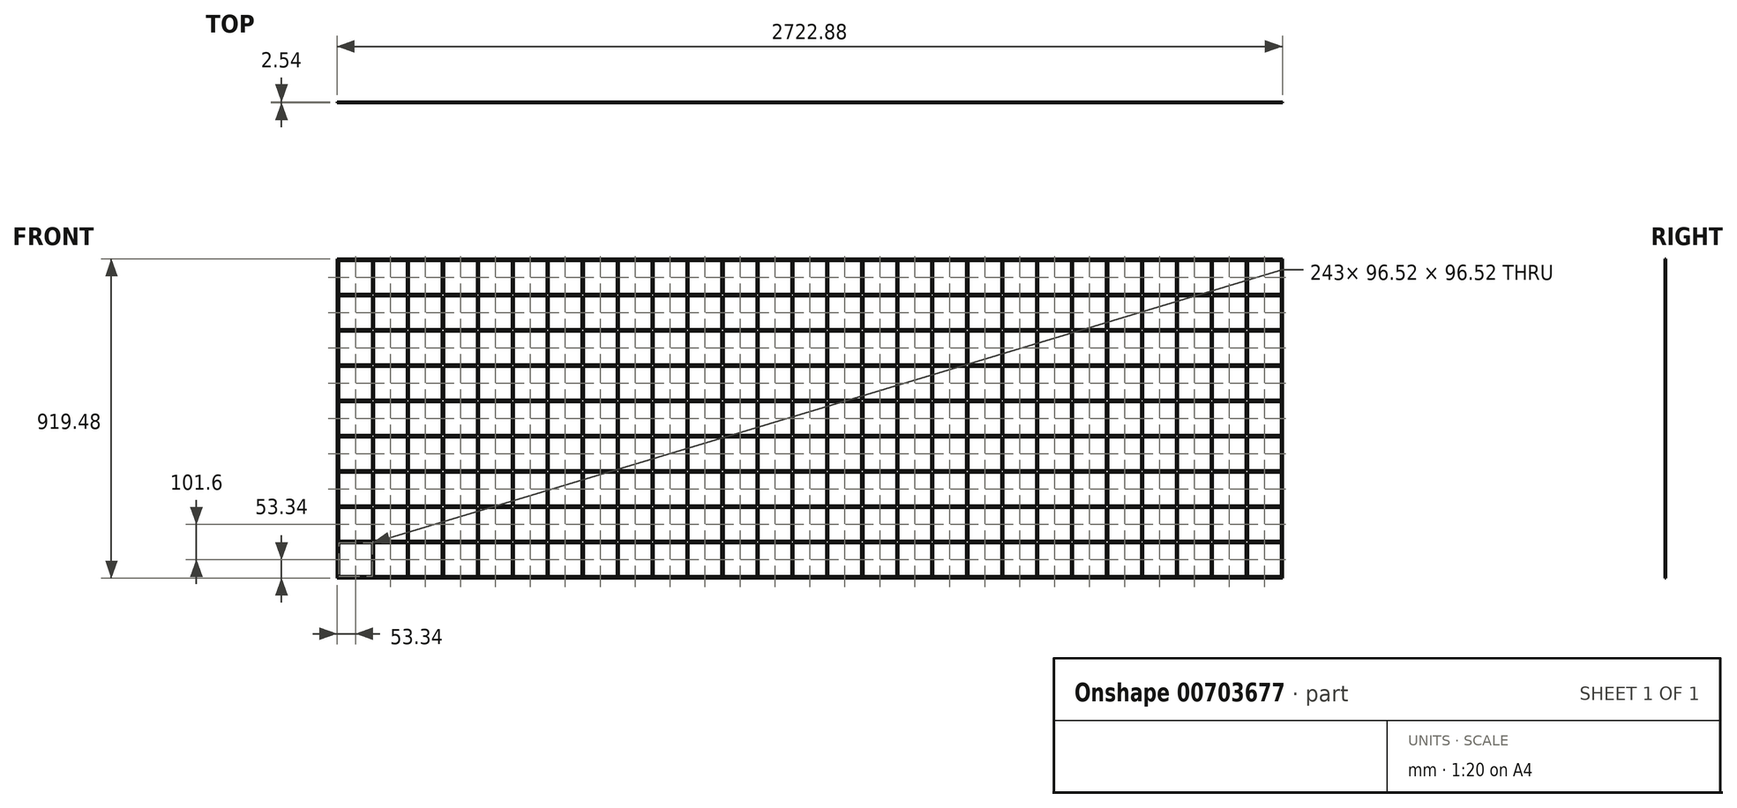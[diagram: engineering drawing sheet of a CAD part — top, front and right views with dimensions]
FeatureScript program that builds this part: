
annotation { "Feature Type Name" : "Feature", "Feature Type Description" : "" }
export const myFeature = defineFeature(function(context is Context, id is Id, definition is map)
    precondition{}
    {
        {
            var Q0;
            Q0=qCreatedBy(makeId("Front.planeOp"),FACE);
            var sketch = newSketch(context, id + "F0", { "sketchPlane" : qUnion([Q0])});
            skLineSegment(sketch, "E0.bottom", {"start": v(0, 0) * mm, "end": v(2722.88, 0) * mm});
            skLineSegment(sketch, "E0.top", {"start": v(0, 919.48) * mm, "end": v(2722.88, 919.48) * mm});
            skLineSegment(sketch, "E0.left", {"start": v(0, 0) * mm, "end": v(0, 919.48) * mm});
            skLineSegment(sketch, "E0.right", {"start": v(2722.88, 0) * mm, "end": v(2722.88, 919.48) * mm});
            skSolve(sketch);
        }
        {
            var Q0;
            Q0=qSketchRegion(id+"F0",true);
            extrude(context, id + "F1", {"entities" : qUnion([Q0]), "depth" : 2.54 * mm, "offsetDistance" : 25.4 * mm});
        }
        {
            var Q0;
            Q0=makeQuery(id+"F0.imprint","IMPRINT",FACE,{"disambiguationData":[TD([[makeQuery(id+"F0.imprint","IMPRINT",EDGE,{"derivedFrom":sQuery(id+"F0.wireOp",EDGE,"E0.bottom")}),1.0]])]});
            var sketch = newSketch(context, id + "F2", { "sketchPlane" : qUnion([Q0])});
            skLineSegment(sketch, "E1.bottom", {"start": v(5.08, 914.4) * mm, "end": v(101.6, 914.4) * mm});
            skLineSegment(sketch, "E1.top", {"start": v(5.08, 817.88) * mm, "end": v(101.6, 817.88) * mm});
            skLineSegment(sketch, "E1.left", {"start": v(5.08, 914.4) * mm, "end": v(5.08, 817.88) * mm});
            skLineSegment(sketch, "E1.right", {"start": v(101.6, 914.4) * mm, "end": v(101.6, 817.88) * mm});
            skLineSegment(sketch, "E2.0.1.0", {"start": v(101.6, 812.8) * mm, "end": v(101.6, 716.28) * mm});
            skLineSegment(sketch, "E2.0.1.1", {"start": v(5.08, 812.8) * mm, "end": v(101.6, 812.8) * mm});
            skLineSegment(sketch, "E2.0.1.2", {"start": v(5.08, 812.8) * mm, "end": v(5.08, 716.28) * mm});
            skLineSegment(sketch, "E2.0.1.3", {"start": v(5.08, 716.28) * mm, "end": v(101.6, 716.28) * mm});
            skLineSegment(sketch, "E2.0.2.0", {"start": v(101.6, 711.2) * mm, "end": v(101.6, 614.68) * mm});
            skLineSegment(sketch, "E2.0.2.1", {"start": v(5.08, 711.2) * mm, "end": v(101.6, 711.2) * mm});
            skLineSegment(sketch, "E2.0.2.2", {"start": v(5.08, 711.2) * mm, "end": v(5.08, 614.68) * mm});
            skLineSegment(sketch, "E2.0.2.3", {"start": v(5.08, 614.68) * mm, "end": v(101.6, 614.68) * mm});
            skLineSegment(sketch, "E2.0.3.0", {"start": v(101.6, 609.6) * mm, "end": v(101.6, 513.08) * mm});
            skLineSegment(sketch, "E2.0.3.1", {"start": v(5.08, 609.6) * mm, "end": v(101.6, 609.6) * mm});
            skLineSegment(sketch, "E2.0.3.2", {"start": v(5.08, 609.6) * mm, "end": v(5.08, 513.08) * mm});
            skLineSegment(sketch, "E2.0.3.3", {"start": v(5.08, 513.08) * mm, "end": v(101.6, 513.08) * mm});
            skLineSegment(sketch, "E2.0.4.0", {"start": v(101.6, 508) * mm, "end": v(101.6, 411.48) * mm});
            skLineSegment(sketch, "E2.0.4.1", {"start": v(5.08, 508) * mm, "end": v(101.6, 508) * mm});
            skLineSegment(sketch, "E2.0.4.2", {"start": v(5.08, 508) * mm, "end": v(5.08, 411.48) * mm});
            skLineSegment(sketch, "E2.0.4.3", {"start": v(5.08, 411.48) * mm, "end": v(101.6, 411.48) * mm});
            skLineSegment(sketch, "E2.0.5.0", {"start": v(101.6, 406.4) * mm, "end": v(101.6, 309.88) * mm});
            skLineSegment(sketch, "E2.0.5.1", {"start": v(5.08, 406.4) * mm, "end": v(101.6, 406.4) * mm});
            skLineSegment(sketch, "E2.0.5.2", {"start": v(5.08, 406.4) * mm, "end": v(5.08, 309.88) * mm});
            skLineSegment(sketch, "E2.0.5.3", {"start": v(5.08, 309.88) * mm, "end": v(101.6, 309.88) * mm});
            skLineSegment(sketch, "E2.0.6.0", {"start": v(101.6, 304.8) * mm, "end": v(101.6, 208.28) * mm});
            skLineSegment(sketch, "E2.0.6.1", {"start": v(5.08, 304.8) * mm, "end": v(101.6, 304.8) * mm});
            skLineSegment(sketch, "E2.0.6.2", {"start": v(5.08, 304.8) * mm, "end": v(5.08, 208.28) * mm});
            skLineSegment(sketch, "E2.0.6.3", {"start": v(5.08, 208.28) * mm, "end": v(101.6, 208.28) * mm});
            skLineSegment(sketch, "E2.0.7.0", {"start": v(101.6, 203.2) * mm, "end": v(101.6, 106.68) * mm});
            skLineSegment(sketch, "E2.0.7.1", {"start": v(5.08, 203.2) * mm, "end": v(101.6, 203.2) * mm});
            skLineSegment(sketch, "E2.0.7.2", {"start": v(5.08, 203.2) * mm, "end": v(5.08, 106.68) * mm});
            skLineSegment(sketch, "E2.0.7.3", {"start": v(5.08, 106.68) * mm, "end": v(101.6, 106.68) * mm});
            skLineSegment(sketch, "E2.0.8.0", {"start": v(101.6, 101.6) * mm, "end": v(101.6, 5.08) * mm});
            skLineSegment(sketch, "E2.0.8.1", {"start": v(5.08, 101.6) * mm, "end": v(101.6, 101.6) * mm});
            skLineSegment(sketch, "E2.0.8.2", {"start": v(5.08, 101.6) * mm, "end": v(5.08, 5.08) * mm});
            skLineSegment(sketch, "E2.0.8.3", {"start": v(5.08, 5.08) * mm, "end": v(101.6, 5.08) * mm});
            skLineSegment(sketch, "E2.1.0.0", {"start": v(202.26, 914.4) * mm, "end": v(202.26, 817.88) * mm});
            skLineSegment(sketch, "E2.1.0.1", {"start": v(105.74, 914.4) * mm, "end": v(202.26, 914.4) * mm});
            skLineSegment(sketch, "E2.1.0.2", {"start": v(105.74, 914.4) * mm, "end": v(105.74, 817.88) * mm});
            skLineSegment(sketch, "E2.1.0.3", {"start": v(105.74, 817.88) * mm, "end": v(202.26, 817.88) * mm});
            skLineSegment(sketch, "E2.1.1.0", {"start": v(202.26, 812.8) * mm, "end": v(202.26, 716.28) * mm});
            skLineSegment(sketch, "E2.1.1.1", {"start": v(105.74, 812.8) * mm, "end": v(202.26, 812.8) * mm});
            skLineSegment(sketch, "E2.1.1.2", {"start": v(105.74, 812.8) * mm, "end": v(105.74, 716.28) * mm});
            skLineSegment(sketch, "E2.1.1.3", {"start": v(105.74, 716.28) * mm, "end": v(202.26, 716.28) * mm});
            skLineSegment(sketch, "E2.1.2.0", {"start": v(202.26, 711.2) * mm, "end": v(202.26, 614.68) * mm});
            skLineSegment(sketch, "E2.1.2.1", {"start": v(105.74, 711.2) * mm, "end": v(202.26, 711.2) * mm});
            skLineSegment(sketch, "E2.1.2.2", {"start": v(105.74, 711.2) * mm, "end": v(105.74, 614.68) * mm});
            skLineSegment(sketch, "E2.1.2.3", {"start": v(105.74, 614.68) * mm, "end": v(202.26, 614.68) * mm});
            skLineSegment(sketch, "E2.1.3.0", {"start": v(202.26, 609.6) * mm, "end": v(202.26, 513.08) * mm});
            skLineSegment(sketch, "E2.1.3.1", {"start": v(105.74, 609.6) * mm, "end": v(202.26, 609.6) * mm});
            skLineSegment(sketch, "E2.1.3.2", {"start": v(105.74, 609.6) * mm, "end": v(105.74, 513.08) * mm});
            skLineSegment(sketch, "E2.1.3.3", {"start": v(105.74, 513.08) * mm, "end": v(202.26, 513.08) * mm});
            skLineSegment(sketch, "E2.1.4.0", {"start": v(202.26, 508) * mm, "end": v(202.26, 411.48) * mm});
            skLineSegment(sketch, "E2.1.4.1", {"start": v(105.74, 508) * mm, "end": v(202.26, 508) * mm});
            skLineSegment(sketch, "E2.1.4.2", {"start": v(105.74, 508) * mm, "end": v(105.74, 411.48) * mm});
            skLineSegment(sketch, "E2.1.4.3", {"start": v(105.74, 411.48) * mm, "end": v(202.26, 411.48) * mm});
            skLineSegment(sketch, "E2.1.5.0", {"start": v(202.26, 406.4) * mm, "end": v(202.26, 309.88) * mm});
            skLineSegment(sketch, "E2.1.5.1", {"start": v(105.74, 406.4) * mm, "end": v(202.26, 406.4) * mm});
            skLineSegment(sketch, "E2.1.5.2", {"start": v(105.74, 406.4) * mm, "end": v(105.74, 309.88) * mm});
            skLineSegment(sketch, "E2.1.5.3", {"start": v(105.74, 309.88) * mm, "end": v(202.26, 309.88) * mm});
            skLineSegment(sketch, "E2.1.6.0", {"start": v(202.26, 304.8) * mm, "end": v(202.26, 208.28) * mm});
            skLineSegment(sketch, "E2.1.6.1", {"start": v(105.74, 304.8) * mm, "end": v(202.26, 304.8) * mm});
            skLineSegment(sketch, "E2.1.6.2", {"start": v(105.74, 304.8) * mm, "end": v(105.74, 208.28) * mm});
            skLineSegment(sketch, "E2.1.6.3", {"start": v(105.74, 208.28) * mm, "end": v(202.26, 208.28) * mm});
            skLineSegment(sketch, "E2.1.7.0", {"start": v(202.26, 203.2) * mm, "end": v(202.26, 106.68) * mm});
            skLineSegment(sketch, "E2.1.7.1", {"start": v(105.74, 203.2) * mm, "end": v(202.26, 203.2) * mm});
            skLineSegment(sketch, "E2.1.7.2", {"start": v(105.74, 203.2) * mm, "end": v(105.74, 106.68) * mm});
            skLineSegment(sketch, "E2.1.7.3", {"start": v(105.74, 106.68) * mm, "end": v(202.26, 106.68) * mm});
            skLineSegment(sketch, "E2.1.8.0", {"start": v(202.26, 101.6) * mm, "end": v(202.26, 5.08) * mm});
            skLineSegment(sketch, "E2.1.8.1", {"start": v(105.74, 101.6) * mm, "end": v(202.26, 101.6) * mm});
            skLineSegment(sketch, "E2.1.8.2", {"start": v(105.74, 101.6) * mm, "end": v(105.74, 5.08) * mm});
            skLineSegment(sketch, "E2.1.8.3", {"start": v(105.74, 5.08) * mm, "end": v(202.26, 5.08) * mm});
            skLineSegment(sketch, "E2.2.0.0", {"start": v(302.92, 914.4) * mm, "end": v(302.92, 817.88) * mm});
            skLineSegment(sketch, "E2.2.0.1", {"start": v(206.4, 914.4) * mm, "end": v(302.92, 914.4) * mm});
            skLineSegment(sketch, "E2.2.0.2", {"start": v(206.4, 914.4) * mm, "end": v(206.4, 817.88) * mm});
            skLineSegment(sketch, "E2.2.0.3", {"start": v(206.4, 817.88) * mm, "end": v(302.92, 817.88) * mm});
            skLineSegment(sketch, "E2.2.1.0", {"start": v(302.92, 812.8) * mm, "end": v(302.92, 716.28) * mm});
            skLineSegment(sketch, "E2.2.1.1", {"start": v(206.4, 812.8) * mm, "end": v(302.92, 812.8) * mm});
            skLineSegment(sketch, "E2.2.1.2", {"start": v(206.4, 812.8) * mm, "end": v(206.4, 716.28) * mm});
            skLineSegment(sketch, "E2.2.1.3", {"start": v(206.4, 716.28) * mm, "end": v(302.92, 716.28) * mm});
            skLineSegment(sketch, "E2.2.2.0", {"start": v(302.92, 711.2) * mm, "end": v(302.92, 614.68) * mm});
            skLineSegment(sketch, "E2.2.2.1", {"start": v(206.4, 711.2) * mm, "end": v(302.92, 711.2) * mm});
            skLineSegment(sketch, "E2.2.2.2", {"start": v(206.4, 711.2) * mm, "end": v(206.4, 614.68) * mm});
            skLineSegment(sketch, "E2.2.2.3", {"start": v(206.4, 614.68) * mm, "end": v(302.92, 614.68) * mm});
            skLineSegment(sketch, "E2.2.3.0", {"start": v(302.92, 609.6) * mm, "end": v(302.92, 513.08) * mm});
            skLineSegment(sketch, "E2.2.3.1", {"start": v(206.4, 609.6) * mm, "end": v(302.92, 609.6) * mm});
            skLineSegment(sketch, "E2.2.3.2", {"start": v(206.4, 609.6) * mm, "end": v(206.4, 513.08) * mm});
            skLineSegment(sketch, "E2.2.3.3", {"start": v(206.4, 513.08) * mm, "end": v(302.92, 513.08) * mm});
            skLineSegment(sketch, "E2.2.4.0", {"start": v(302.92, 508) * mm, "end": v(302.92, 411.48) * mm});
            skLineSegment(sketch, "E2.2.4.1", {"start": v(206.4, 508) * mm, "end": v(302.92, 508) * mm});
            skLineSegment(sketch, "E2.2.4.2", {"start": v(206.4, 508) * mm, "end": v(206.4, 411.48) * mm});
            skLineSegment(sketch, "E2.2.4.3", {"start": v(206.4, 411.48) * mm, "end": v(302.92, 411.48) * mm});
            skLineSegment(sketch, "E2.2.5.0", {"start": v(302.92, 406.4) * mm, "end": v(302.92, 309.88) * mm});
            skLineSegment(sketch, "E2.2.5.1", {"start": v(206.4, 406.4) * mm, "end": v(302.92, 406.4) * mm});
            skLineSegment(sketch, "E2.2.5.2", {"start": v(206.4, 406.4) * mm, "end": v(206.4, 309.88) * mm});
            skLineSegment(sketch, "E2.2.5.3", {"start": v(206.4, 309.88) * mm, "end": v(302.92, 309.88) * mm});
            skLineSegment(sketch, "E2.2.6.0", {"start": v(302.92, 304.8) * mm, "end": v(302.92, 208.28) * mm});
            skLineSegment(sketch, "E2.2.6.1", {"start": v(206.4, 304.8) * mm, "end": v(302.92, 304.8) * mm});
            skLineSegment(sketch, "E2.2.6.2", {"start": v(206.4, 304.8) * mm, "end": v(206.4, 208.28) * mm});
            skLineSegment(sketch, "E2.2.6.3", {"start": v(206.4, 208.28) * mm, "end": v(302.92, 208.28) * mm});
            skLineSegment(sketch, "E2.2.7.0", {"start": v(302.92, 203.2) * mm, "end": v(302.92, 106.68) * mm});
            skLineSegment(sketch, "E2.2.7.1", {"start": v(206.4, 203.2) * mm, "end": v(302.92, 203.2) * mm});
            skLineSegment(sketch, "E2.2.7.2", {"start": v(206.4, 203.2) * mm, "end": v(206.4, 106.68) * mm});
            skLineSegment(sketch, "E2.2.7.3", {"start": v(206.4, 106.68) * mm, "end": v(302.92, 106.68) * mm});
            skLineSegment(sketch, "E2.2.8.0", {"start": v(302.92, 101.6) * mm, "end": v(302.92, 5.08) * mm});
            skLineSegment(sketch, "E2.2.8.1", {"start": v(206.4, 101.6) * mm, "end": v(302.92, 101.6) * mm});
            skLineSegment(sketch, "E2.2.8.2", {"start": v(206.4, 101.6) * mm, "end": v(206.4, 5.08) * mm});
            skLineSegment(sketch, "E2.2.8.3", {"start": v(206.4, 5.08) * mm, "end": v(302.92, 5.08) * mm});
            skLineSegment(sketch, "E2.3.0.0", {"start": v(403.58, 914.4) * mm, "end": v(403.58, 817.88) * mm});
            skLineSegment(sketch, "E2.3.0.1", {"start": v(307.06, 914.4) * mm, "end": v(403.58, 914.4) * mm});
            skLineSegment(sketch, "E2.3.0.2", {"start": v(307.06, 914.4) * mm, "end": v(307.06, 817.88) * mm});
            skLineSegment(sketch, "E2.3.0.3", {"start": v(307.06, 817.88) * mm, "end": v(403.58, 817.88) * mm});
            skLineSegment(sketch, "E2.3.1.0", {"start": v(403.58, 812.8) * mm, "end": v(403.58, 716.28) * mm});
            skLineSegment(sketch, "E2.3.1.1", {"start": v(307.06, 812.8) * mm, "end": v(403.58, 812.8) * mm});
            skLineSegment(sketch, "E2.3.1.2", {"start": v(307.06, 812.8) * mm, "end": v(307.06, 716.28) * mm});
            skLineSegment(sketch, "E2.3.1.3", {"start": v(307.06, 716.28) * mm, "end": v(403.58, 716.28) * mm});
            skLineSegment(sketch, "E2.3.2.0", {"start": v(403.58, 711.2) * mm, "end": v(403.58, 614.68) * mm});
            skLineSegment(sketch, "E2.3.2.1", {"start": v(307.06, 711.2) * mm, "end": v(403.58, 711.2) * mm});
            skLineSegment(sketch, "E2.3.2.2", {"start": v(307.06, 711.2) * mm, "end": v(307.06, 614.68) * mm});
            skLineSegment(sketch, "E2.3.2.3", {"start": v(307.06, 614.68) * mm, "end": v(403.58, 614.68) * mm});
            skLineSegment(sketch, "E2.3.3.0", {"start": v(403.58, 609.6) * mm, "end": v(403.58, 513.08) * mm});
            skLineSegment(sketch, "E2.3.3.1", {"start": v(307.06, 609.6) * mm, "end": v(403.58, 609.6) * mm});
            skLineSegment(sketch, "E2.3.3.2", {"start": v(307.06, 609.6) * mm, "end": v(307.06, 513.08) * mm});
            skLineSegment(sketch, "E2.3.3.3", {"start": v(307.06, 513.08) * mm, "end": v(403.58, 513.08) * mm});
            skLineSegment(sketch, "E2.3.4.0", {"start": v(403.58, 508) * mm, "end": v(403.58, 411.48) * mm});
            skLineSegment(sketch, "E2.3.4.1", {"start": v(307.06, 508) * mm, "end": v(403.58, 508) * mm});
            skLineSegment(sketch, "E2.3.4.2", {"start": v(307.06, 508) * mm, "end": v(307.06, 411.48) * mm});
            skLineSegment(sketch, "E2.3.4.3", {"start": v(307.06, 411.48) * mm, "end": v(403.58, 411.48) * mm});
            skLineSegment(sketch, "E2.3.5.0", {"start": v(403.58, 406.4) * mm, "end": v(403.58, 309.88) * mm});
            skLineSegment(sketch, "E2.3.5.1", {"start": v(307.06, 406.4) * mm, "end": v(403.58, 406.4) * mm});
            skLineSegment(sketch, "E2.3.5.2", {"start": v(307.06, 406.4) * mm, "end": v(307.06, 309.88) * mm});
            skLineSegment(sketch, "E2.3.5.3", {"start": v(307.06, 309.88) * mm, "end": v(403.58, 309.88) * mm});
            skLineSegment(sketch, "E2.3.6.0", {"start": v(403.58, 304.8) * mm, "end": v(403.58, 208.28) * mm});
            skLineSegment(sketch, "E2.3.6.1", {"start": v(307.06, 304.8) * mm, "end": v(403.58, 304.8) * mm});
            skLineSegment(sketch, "E2.3.6.2", {"start": v(307.06, 304.8) * mm, "end": v(307.06, 208.28) * mm});
            skLineSegment(sketch, "E2.3.6.3", {"start": v(307.06, 208.28) * mm, "end": v(403.58, 208.28) * mm});
            skLineSegment(sketch, "E2.3.7.0", {"start": v(403.58, 203.2) * mm, "end": v(403.58, 106.68) * mm});
            skLineSegment(sketch, "E2.3.7.1", {"start": v(307.06, 203.2) * mm, "end": v(403.58, 203.2) * mm});
            skLineSegment(sketch, "E2.3.7.2", {"start": v(307.06, 203.2) * mm, "end": v(307.06, 106.68) * mm});
            skLineSegment(sketch, "E2.3.7.3", {"start": v(307.06, 106.68) * mm, "end": v(403.58, 106.68) * mm});
            skLineSegment(sketch, "E2.3.8.0", {"start": v(403.58, 101.6) * mm, "end": v(403.58, 5.08) * mm});
            skLineSegment(sketch, "E2.3.8.1", {"start": v(307.06, 101.6) * mm, "end": v(403.58, 101.6) * mm});
            skLineSegment(sketch, "E2.3.8.2", {"start": v(307.06, 101.6) * mm, "end": v(307.06, 5.08) * mm});
            skLineSegment(sketch, "E2.3.8.3", {"start": v(307.06, 5.08) * mm, "end": v(403.58, 5.08) * mm});
            skLineSegment(sketch, "E2.4.0.0", {"start": v(504.24, 914.4) * mm, "end": v(504.24, 817.88) * mm});
            skLineSegment(sketch, "E2.4.0.1", {"start": v(407.72, 914.4) * mm, "end": v(504.24, 914.4) * mm});
            skLineSegment(sketch, "E2.4.0.2", {"start": v(407.72, 914.4) * mm, "end": v(407.72, 817.88) * mm});
            skLineSegment(sketch, "E2.4.0.3", {"start": v(407.72, 817.88) * mm, "end": v(504.24, 817.88) * mm});
            skLineSegment(sketch, "E2.4.1.0", {"start": v(504.24, 812.8) * mm, "end": v(504.24, 716.28) * mm});
            skLineSegment(sketch, "E2.4.1.1", {"start": v(407.72, 812.8) * mm, "end": v(504.24, 812.8) * mm});
            skLineSegment(sketch, "E2.4.1.2", {"start": v(407.72, 812.8) * mm, "end": v(407.72, 716.28) * mm});
            skLineSegment(sketch, "E2.4.1.3", {"start": v(407.72, 716.28) * mm, "end": v(504.24, 716.28) * mm});
            skLineSegment(sketch, "E2.4.2.0", {"start": v(504.24, 711.2) * mm, "end": v(504.24, 614.68) * mm});
            skLineSegment(sketch, "E2.4.2.1", {"start": v(407.72, 711.2) * mm, "end": v(504.24, 711.2) * mm});
            skLineSegment(sketch, "E2.4.2.2", {"start": v(407.72, 711.2) * mm, "end": v(407.72, 614.68) * mm});
            skLineSegment(sketch, "E2.4.2.3", {"start": v(407.72, 614.68) * mm, "end": v(504.24, 614.68) * mm});
            skLineSegment(sketch, "E2.4.3.0", {"start": v(504.24, 609.6) * mm, "end": v(504.24, 513.08) * mm});
            skLineSegment(sketch, "E2.4.3.1", {"start": v(407.72, 609.6) * mm, "end": v(504.24, 609.6) * mm});
            skLineSegment(sketch, "E2.4.3.2", {"start": v(407.72, 609.6) * mm, "end": v(407.72, 513.08) * mm});
            skLineSegment(sketch, "E2.4.3.3", {"start": v(407.72, 513.08) * mm, "end": v(504.24, 513.08) * mm});
            skLineSegment(sketch, "E2.4.4.0", {"start": v(504.24, 508) * mm, "end": v(504.24, 411.48) * mm});
            skLineSegment(sketch, "E2.4.4.1", {"start": v(407.72, 508) * mm, "end": v(504.24, 508) * mm});
            skLineSegment(sketch, "E2.4.4.2", {"start": v(407.72, 508) * mm, "end": v(407.72, 411.48) * mm});
            skLineSegment(sketch, "E2.4.4.3", {"start": v(407.72, 411.48) * mm, "end": v(504.24, 411.48) * mm});
            skLineSegment(sketch, "E2.4.5.0", {"start": v(504.24, 406.4) * mm, "end": v(504.24, 309.88) * mm});
            skLineSegment(sketch, "E2.4.5.1", {"start": v(407.72, 406.4) * mm, "end": v(504.24, 406.4) * mm});
            skLineSegment(sketch, "E2.4.5.2", {"start": v(407.72, 406.4) * mm, "end": v(407.72, 309.88) * mm});
            skLineSegment(sketch, "E2.4.5.3", {"start": v(407.72, 309.88) * mm, "end": v(504.24, 309.88) * mm});
            skLineSegment(sketch, "E2.4.6.0", {"start": v(504.24, 304.8) * mm, "end": v(504.24, 208.28) * mm});
            skLineSegment(sketch, "E2.4.6.1", {"start": v(407.72, 304.8) * mm, "end": v(504.24, 304.8) * mm});
            skLineSegment(sketch, "E2.4.6.2", {"start": v(407.72, 304.8) * mm, "end": v(407.72, 208.28) * mm});
            skLineSegment(sketch, "E2.4.6.3", {"start": v(407.72, 208.28) * mm, "end": v(504.24, 208.28) * mm});
            skLineSegment(sketch, "E2.4.7.0", {"start": v(504.24, 203.2) * mm, "end": v(504.24, 106.68) * mm});
            skLineSegment(sketch, "E2.4.7.1", {"start": v(407.72, 203.2) * mm, "end": v(504.24, 203.2) * mm});
            skLineSegment(sketch, "E2.4.7.2", {"start": v(407.72, 203.2) * mm, "end": v(407.72, 106.68) * mm});
            skLineSegment(sketch, "E2.4.7.3", {"start": v(407.72, 106.68) * mm, "end": v(504.24, 106.68) * mm});
            skLineSegment(sketch, "E2.4.8.0", {"start": v(504.24, 101.6) * mm, "end": v(504.24, 5.08) * mm});
            skLineSegment(sketch, "E2.4.8.1", {"start": v(407.72, 101.6) * mm, "end": v(504.24, 101.6) * mm});
            skLineSegment(sketch, "E2.4.8.2", {"start": v(407.72, 101.6) * mm, "end": v(407.72, 5.08) * mm});
            skLineSegment(sketch, "E2.4.8.3", {"start": v(407.72, 5.08) * mm, "end": v(504.24, 5.08) * mm});
            skLineSegment(sketch, "E2.5.0.0", {"start": v(604.9, 914.4) * mm, "end": v(604.9, 817.88) * mm});
            skLineSegment(sketch, "E2.5.0.1", {"start": v(508.38, 914.4) * mm, "end": v(604.9, 914.4) * mm});
            skLineSegment(sketch, "E2.5.0.2", {"start": v(508.38, 914.4) * mm, "end": v(508.38, 817.88) * mm});
            skLineSegment(sketch, "E2.5.0.3", {"start": v(508.38, 817.88) * mm, "end": v(604.9, 817.88) * mm});
            skLineSegment(sketch, "E2.5.1.0", {"start": v(604.9, 812.8) * mm, "end": v(604.9, 716.28) * mm});
            skLineSegment(sketch, "E2.5.1.1", {"start": v(508.38, 812.8) * mm, "end": v(604.9, 812.8) * mm});
            skLineSegment(sketch, "E2.5.1.2", {"start": v(508.38, 812.8) * mm, "end": v(508.38, 716.28) * mm});
            skLineSegment(sketch, "E2.5.1.3", {"start": v(508.38, 716.28) * mm, "end": v(604.9, 716.28) * mm});
            skLineSegment(sketch, "E2.5.2.0", {"start": v(604.9, 711.2) * mm, "end": v(604.9, 614.68) * mm});
            skLineSegment(sketch, "E2.5.2.1", {"start": v(508.38, 711.2) * mm, "end": v(604.9, 711.2) * mm});
            skLineSegment(sketch, "E2.5.2.2", {"start": v(508.38, 711.2) * mm, "end": v(508.38, 614.68) * mm});
            skLineSegment(sketch, "E2.5.2.3", {"start": v(508.38, 614.68) * mm, "end": v(604.9, 614.68) * mm});
            skLineSegment(sketch, "E2.5.3.0", {"start": v(604.9, 609.6) * mm, "end": v(604.9, 513.08) * mm});
            skLineSegment(sketch, "E2.5.3.1", {"start": v(508.38, 609.6) * mm, "end": v(604.9, 609.6) * mm});
            skLineSegment(sketch, "E2.5.3.2", {"start": v(508.38, 609.6) * mm, "end": v(508.38, 513.08) * mm});
            skLineSegment(sketch, "E2.5.3.3", {"start": v(508.38, 513.08) * mm, "end": v(604.9, 513.08) * mm});
            skLineSegment(sketch, "E2.5.4.0", {"start": v(604.9, 508) * mm, "end": v(604.9, 411.48) * mm});
            skLineSegment(sketch, "E2.5.4.1", {"start": v(508.38, 508) * mm, "end": v(604.9, 508) * mm});
            skLineSegment(sketch, "E2.5.4.2", {"start": v(508.38, 508) * mm, "end": v(508.38, 411.48) * mm});
            skLineSegment(sketch, "E2.5.4.3", {"start": v(508.38, 411.48) * mm, "end": v(604.9, 411.48) * mm});
            skLineSegment(sketch, "E2.5.5.0", {"start": v(604.9, 406.4) * mm, "end": v(604.9, 309.88) * mm});
            skLineSegment(sketch, "E2.5.5.1", {"start": v(508.38, 406.4) * mm, "end": v(604.9, 406.4) * mm});
            skLineSegment(sketch, "E2.5.5.2", {"start": v(508.38, 406.4) * mm, "end": v(508.38, 309.88) * mm});
            skLineSegment(sketch, "E2.5.5.3", {"start": v(508.38, 309.88) * mm, "end": v(604.9, 309.88) * mm});
            skLineSegment(sketch, "E2.5.6.0", {"start": v(604.9, 304.8) * mm, "end": v(604.9, 208.28) * mm});
            skLineSegment(sketch, "E2.5.6.1", {"start": v(508.38, 304.8) * mm, "end": v(604.9, 304.8) * mm});
            skLineSegment(sketch, "E2.5.6.2", {"start": v(508.38, 304.8) * mm, "end": v(508.38, 208.28) * mm});
            skLineSegment(sketch, "E2.5.6.3", {"start": v(508.38, 208.28) * mm, "end": v(604.9, 208.28) * mm});
            skLineSegment(sketch, "E2.5.7.0", {"start": v(604.9, 203.2) * mm, "end": v(604.9, 106.68) * mm});
            skLineSegment(sketch, "E2.5.7.1", {"start": v(508.38, 203.2) * mm, "end": v(604.9, 203.2) * mm});
            skLineSegment(sketch, "E2.5.7.2", {"start": v(508.38, 203.2) * mm, "end": v(508.38, 106.68) * mm});
            skLineSegment(sketch, "E2.5.7.3", {"start": v(508.38, 106.68) * mm, "end": v(604.9, 106.68) * mm});
            skLineSegment(sketch, "E2.5.8.0", {"start": v(604.9, 101.6) * mm, "end": v(604.9, 5.08) * mm});
            skLineSegment(sketch, "E2.5.8.1", {"start": v(508.38, 101.6) * mm, "end": v(604.9, 101.6) * mm});
            skLineSegment(sketch, "E2.5.8.2", {"start": v(508.38, 101.6) * mm, "end": v(508.38, 5.08) * mm});
            skLineSegment(sketch, "E2.5.8.3", {"start": v(508.38, 5.08) * mm, "end": v(604.9, 5.08) * mm});
            skLineSegment(sketch, "E2.6.0.0", {"start": v(705.56, 914.4) * mm, "end": v(705.56, 817.88) * mm});
            skLineSegment(sketch, "E2.6.0.1", {"start": v(609.04, 914.4) * mm, "end": v(705.56, 914.4) * mm});
            skLineSegment(sketch, "E2.6.0.2", {"start": v(609.04, 914.4) * mm, "end": v(609.04, 817.88) * mm});
            skLineSegment(sketch, "E2.6.0.3", {"start": v(609.04, 817.88) * mm, "end": v(705.56, 817.88) * mm});
            skLineSegment(sketch, "E2.6.1.0", {"start": v(705.56, 812.8) * mm, "end": v(705.56, 716.28) * mm});
            skLineSegment(sketch, "E2.6.1.1", {"start": v(609.04, 812.8) * mm, "end": v(705.56, 812.8) * mm});
            skLineSegment(sketch, "E2.6.1.2", {"start": v(609.04, 812.8) * mm, "end": v(609.04, 716.28) * mm});
            skLineSegment(sketch, "E2.6.1.3", {"start": v(609.04, 716.28) * mm, "end": v(705.56, 716.28) * mm});
            skLineSegment(sketch, "E2.6.2.0", {"start": v(705.56, 711.2) * mm, "end": v(705.56, 614.68) * mm});
            skLineSegment(sketch, "E2.6.2.1", {"start": v(609.04, 711.2) * mm, "end": v(705.56, 711.2) * mm});
            skLineSegment(sketch, "E2.6.2.2", {"start": v(609.04, 711.2) * mm, "end": v(609.04, 614.68) * mm});
            skLineSegment(sketch, "E2.6.2.3", {"start": v(609.04, 614.68) * mm, "end": v(705.56, 614.68) * mm});
            skLineSegment(sketch, "E2.6.3.0", {"start": v(705.56, 609.6) * mm, "end": v(705.56, 513.08) * mm});
            skLineSegment(sketch, "E2.6.3.1", {"start": v(609.04, 609.6) * mm, "end": v(705.56, 609.6) * mm});
            skLineSegment(sketch, "E2.6.3.2", {"start": v(609.04, 609.6) * mm, "end": v(609.04, 513.08) * mm});
            skLineSegment(sketch, "E2.6.3.3", {"start": v(609.04, 513.08) * mm, "end": v(705.56, 513.08) * mm});
            skLineSegment(sketch, "E2.6.4.0", {"start": v(705.56, 508) * mm, "end": v(705.56, 411.48) * mm});
            skLineSegment(sketch, "E2.6.4.1", {"start": v(609.04, 508) * mm, "end": v(705.56, 508) * mm});
            skLineSegment(sketch, "E2.6.4.2", {"start": v(609.04, 508) * mm, "end": v(609.04, 411.48) * mm});
            skLineSegment(sketch, "E2.6.4.3", {"start": v(609.04, 411.48) * mm, "end": v(705.56, 411.48) * mm});
            skLineSegment(sketch, "E2.6.5.0", {"start": v(705.56, 406.4) * mm, "end": v(705.56, 309.88) * mm});
            skLineSegment(sketch, "E2.6.5.1", {"start": v(609.04, 406.4) * mm, "end": v(705.56, 406.4) * mm});
            skLineSegment(sketch, "E2.6.5.2", {"start": v(609.04, 406.4) * mm, "end": v(609.04, 309.88) * mm});
            skLineSegment(sketch, "E2.6.5.3", {"start": v(609.04, 309.88) * mm, "end": v(705.56, 309.88) * mm});
            skLineSegment(sketch, "E2.6.6.0", {"start": v(705.56, 304.8) * mm, "end": v(705.56, 208.28) * mm});
            skLineSegment(sketch, "E2.6.6.1", {"start": v(609.04, 304.8) * mm, "end": v(705.56, 304.8) * mm});
            skLineSegment(sketch, "E2.6.6.2", {"start": v(609.04, 304.8) * mm, "end": v(609.04, 208.28) * mm});
            skLineSegment(sketch, "E2.6.6.3", {"start": v(609.04, 208.28) * mm, "end": v(705.56, 208.28) * mm});
            skLineSegment(sketch, "E2.6.7.0", {"start": v(705.56, 203.2) * mm, "end": v(705.56, 106.68) * mm});
            skLineSegment(sketch, "E2.6.7.1", {"start": v(609.04, 203.2) * mm, "end": v(705.56, 203.2) * mm});
            skLineSegment(sketch, "E2.6.7.2", {"start": v(609.04, 203.2) * mm, "end": v(609.04, 106.68) * mm});
            skLineSegment(sketch, "E2.6.7.3", {"start": v(609.04, 106.68) * mm, "end": v(705.56, 106.68) * mm});
            skLineSegment(sketch, "E2.6.8.0", {"start": v(705.56, 101.6) * mm, "end": v(705.56, 5.08) * mm});
            skLineSegment(sketch, "E2.6.8.1", {"start": v(609.04, 101.6) * mm, "end": v(705.56, 101.6) * mm});
            skLineSegment(sketch, "E2.6.8.2", {"start": v(609.04, 101.6) * mm, "end": v(609.04, 5.08) * mm});
            skLineSegment(sketch, "E2.6.8.3", {"start": v(609.04, 5.08) * mm, "end": v(705.56, 5.08) * mm});
            skLineSegment(sketch, "E2.7.0.0", {"start": v(806.22, 914.4) * mm, "end": v(806.22, 817.88) * mm});
            skLineSegment(sketch, "E2.7.0.1", {"start": v(709.7, 914.4) * mm, "end": v(806.22, 914.4) * mm});
            skLineSegment(sketch, "E2.7.0.2", {"start": v(709.7, 914.4) * mm, "end": v(709.7, 817.88) * mm});
            skLineSegment(sketch, "E2.7.0.3", {"start": v(709.7, 817.88) * mm, "end": v(806.22, 817.88) * mm});
            skLineSegment(sketch, "E2.7.1.0", {"start": v(806.22, 812.8) * mm, "end": v(806.22, 716.28) * mm});
            skLineSegment(sketch, "E2.7.1.1", {"start": v(709.7, 812.8) * mm, "end": v(806.22, 812.8) * mm});
            skLineSegment(sketch, "E2.7.1.2", {"start": v(709.7, 812.8) * mm, "end": v(709.7, 716.28) * mm});
            skLineSegment(sketch, "E2.7.1.3", {"start": v(709.7, 716.28) * mm, "end": v(806.22, 716.28) * mm});
            skLineSegment(sketch, "E2.7.2.0", {"start": v(806.22, 711.2) * mm, "end": v(806.22, 614.68) * mm});
            skLineSegment(sketch, "E2.7.2.1", {"start": v(709.7, 711.2) * mm, "end": v(806.22, 711.2) * mm});
            skLineSegment(sketch, "E2.7.2.2", {"start": v(709.7, 711.2) * mm, "end": v(709.7, 614.68) * mm});
            skLineSegment(sketch, "E2.7.2.3", {"start": v(709.7, 614.68) * mm, "end": v(806.22, 614.68) * mm});
            skLineSegment(sketch, "E2.7.3.0", {"start": v(806.22, 609.6) * mm, "end": v(806.22, 513.08) * mm});
            skLineSegment(sketch, "E2.7.3.1", {"start": v(709.7, 609.6) * mm, "end": v(806.22, 609.6) * mm});
            skLineSegment(sketch, "E2.7.3.2", {"start": v(709.7, 609.6) * mm, "end": v(709.7, 513.08) * mm});
            skLineSegment(sketch, "E2.7.3.3", {"start": v(709.7, 513.08) * mm, "end": v(806.22, 513.08) * mm});
            skLineSegment(sketch, "E2.7.4.0", {"start": v(806.22, 508) * mm, "end": v(806.22, 411.48) * mm});
            skLineSegment(sketch, "E2.7.4.1", {"start": v(709.7, 508) * mm, "end": v(806.22, 508) * mm});
            skLineSegment(sketch, "E2.7.4.2", {"start": v(709.7, 508) * mm, "end": v(709.7, 411.48) * mm});
            skLineSegment(sketch, "E2.7.4.3", {"start": v(709.7, 411.48) * mm, "end": v(806.22, 411.48) * mm});
            skLineSegment(sketch, "E2.7.5.0", {"start": v(806.22, 406.4) * mm, "end": v(806.22, 309.88) * mm});
            skLineSegment(sketch, "E2.7.5.1", {"start": v(709.7, 406.4) * mm, "end": v(806.22, 406.4) * mm});
            skLineSegment(sketch, "E2.7.5.2", {"start": v(709.7, 406.4) * mm, "end": v(709.7, 309.88) * mm});
            skLineSegment(sketch, "E2.7.5.3", {"start": v(709.7, 309.88) * mm, "end": v(806.22, 309.88) * mm});
            skLineSegment(sketch, "E2.7.6.0", {"start": v(806.22, 304.8) * mm, "end": v(806.22, 208.28) * mm});
            skLineSegment(sketch, "E2.7.6.1", {"start": v(709.7, 304.8) * mm, "end": v(806.22, 304.8) * mm});
            skLineSegment(sketch, "E2.7.6.2", {"start": v(709.7, 304.8) * mm, "end": v(709.7, 208.28) * mm});
            skLineSegment(sketch, "E2.7.6.3", {"start": v(709.7, 208.28) * mm, "end": v(806.22, 208.28) * mm});
            skLineSegment(sketch, "E2.7.7.0", {"start": v(806.22, 203.2) * mm, "end": v(806.22, 106.68) * mm});
            skLineSegment(sketch, "E2.7.7.1", {"start": v(709.7, 203.2) * mm, "end": v(806.22, 203.2) * mm});
            skLineSegment(sketch, "E2.7.7.2", {"start": v(709.7, 203.2) * mm, "end": v(709.7, 106.68) * mm});
            skLineSegment(sketch, "E2.7.7.3", {"start": v(709.7, 106.68) * mm, "end": v(806.22, 106.68) * mm});
            skLineSegment(sketch, "E2.7.8.0", {"start": v(806.22, 101.6) * mm, "end": v(806.22, 5.08) * mm});
            skLineSegment(sketch, "E2.7.8.1", {"start": v(709.7, 101.6) * mm, "end": v(806.22, 101.6) * mm});
            skLineSegment(sketch, "E2.7.8.2", {"start": v(709.7, 101.6) * mm, "end": v(709.7, 5.08) * mm});
            skLineSegment(sketch, "E2.7.8.3", {"start": v(709.7, 5.08) * mm, "end": v(806.22, 5.08) * mm});
            skLineSegment(sketch, "E2.8.0.0", {"start": v(906.88, 914.4) * mm, "end": v(906.88, 817.88) * mm});
            skLineSegment(sketch, "E2.8.0.1", {"start": v(810.36, 914.4) * mm, "end": v(906.88, 914.4) * mm});
            skLineSegment(sketch, "E2.8.0.2", {"start": v(810.36, 914.4) * mm, "end": v(810.36, 817.88) * mm});
            skLineSegment(sketch, "E2.8.0.3", {"start": v(810.36, 817.88) * mm, "end": v(906.88, 817.88) * mm});
            skLineSegment(sketch, "E2.8.1.0", {"start": v(906.88, 812.8) * mm, "end": v(906.88, 716.28) * mm});
            skLineSegment(sketch, "E2.8.1.1", {"start": v(810.36, 812.8) * mm, "end": v(906.88, 812.8) * mm});
            skLineSegment(sketch, "E2.8.1.2", {"start": v(810.36, 812.8) * mm, "end": v(810.36, 716.28) * mm});
            skLineSegment(sketch, "E2.8.1.3", {"start": v(810.36, 716.28) * mm, "end": v(906.88, 716.28) * mm});
            skLineSegment(sketch, "E2.8.2.0", {"start": v(906.88, 711.2) * mm, "end": v(906.88, 614.68) * mm});
            skLineSegment(sketch, "E2.8.2.1", {"start": v(810.36, 711.2) * mm, "end": v(906.88, 711.2) * mm});
            skLineSegment(sketch, "E2.8.2.2", {"start": v(810.36, 711.2) * mm, "end": v(810.36, 614.68) * mm});
            skLineSegment(sketch, "E2.8.2.3", {"start": v(810.36, 614.68) * mm, "end": v(906.88, 614.68) * mm});
            skLineSegment(sketch, "E2.8.3.0", {"start": v(906.88, 609.6) * mm, "end": v(906.88, 513.08) * mm});
            skLineSegment(sketch, "E2.8.3.1", {"start": v(810.36, 609.6) * mm, "end": v(906.88, 609.6) * mm});
            skLineSegment(sketch, "E2.8.3.2", {"start": v(810.36, 609.6) * mm, "end": v(810.36, 513.08) * mm});
            skLineSegment(sketch, "E2.8.3.3", {"start": v(810.36, 513.08) * mm, "end": v(906.88, 513.08) * mm});
            skLineSegment(sketch, "E2.8.4.0", {"start": v(906.88, 508) * mm, "end": v(906.88, 411.48) * mm});
            skLineSegment(sketch, "E2.8.4.1", {"start": v(810.36, 508) * mm, "end": v(906.88, 508) * mm});
            skLineSegment(sketch, "E2.8.4.2", {"start": v(810.36, 508) * mm, "end": v(810.36, 411.48) * mm});
            skLineSegment(sketch, "E2.8.4.3", {"start": v(810.36, 411.48) * mm, "end": v(906.88, 411.48) * mm});
            skLineSegment(sketch, "E2.8.5.0", {"start": v(906.88, 406.4) * mm, "end": v(906.88, 309.88) * mm});
            skLineSegment(sketch, "E2.8.5.1", {"start": v(810.36, 406.4) * mm, "end": v(906.88, 406.4) * mm});
            skLineSegment(sketch, "E2.8.5.2", {"start": v(810.36, 406.4) * mm, "end": v(810.36, 309.88) * mm});
            skLineSegment(sketch, "E2.8.5.3", {"start": v(810.36, 309.88) * mm, "end": v(906.88, 309.88) * mm});
            skLineSegment(sketch, "E2.8.6.0", {"start": v(906.88, 304.8) * mm, "end": v(906.88, 208.28) * mm});
            skLineSegment(sketch, "E2.8.6.1", {"start": v(810.36, 304.8) * mm, "end": v(906.88, 304.8) * mm});
            skLineSegment(sketch, "E2.8.6.2", {"start": v(810.36, 304.8) * mm, "end": v(810.36, 208.28) * mm});
            skLineSegment(sketch, "E2.8.6.3", {"start": v(810.36, 208.28) * mm, "end": v(906.88, 208.28) * mm});
            skLineSegment(sketch, "E2.8.7.0", {"start": v(906.88, 203.2) * mm, "end": v(906.88, 106.68) * mm});
            skLineSegment(sketch, "E2.8.7.1", {"start": v(810.36, 203.2) * mm, "end": v(906.88, 203.2) * mm});
            skLineSegment(sketch, "E2.8.7.2", {"start": v(810.36, 203.2) * mm, "end": v(810.36, 106.68) * mm});
            skLineSegment(sketch, "E2.8.7.3", {"start": v(810.36, 106.68) * mm, "end": v(906.88, 106.68) * mm});
            skLineSegment(sketch, "E2.8.8.0", {"start": v(906.88, 101.6) * mm, "end": v(906.88, 5.08) * mm});
            skLineSegment(sketch, "E2.8.8.1", {"start": v(810.36, 101.6) * mm, "end": v(906.88, 101.6) * mm});
            skLineSegment(sketch, "E2.8.8.2", {"start": v(810.36, 101.6) * mm, "end": v(810.36, 5.08) * mm});
            skLineSegment(sketch, "E2.8.8.3", {"start": v(810.36, 5.08) * mm, "end": v(906.88, 5.08) * mm});
            skLineSegment(sketch, "E2.direction1", {"start": v(101.6, 817.88) * mm, "end": v(202.26, 817.88) * mm, "construction": true});
            skLineSegment(sketch, "E2.direction2", {"start": v(101.6, 817.88) * mm, "end": v(101.6, 716.28) * mm, "construction": true});
            skLineSegment(sketch, "E3.0.9.0", {"start": v(1007.54, 914.4) * mm, "end": v(1007.54, 817.88) * mm});
            skLineSegment(sketch, "E3.3.9.0", {"start": v(911.02, 914.4) * mm, "end": v(1007.54, 914.4) * mm});
            skLineSegment(sketch, "E3.6.9.0", {"start": v(911.02, 914.4) * mm, "end": v(911.02, 817.88) * mm});
            skLineSegment(sketch, "E3.9.9.0", {"start": v(911.02, 817.88) * mm, "end": v(1007.54, 817.88) * mm});
            skLineSegment(sketch, "E3.0.9.1", {"start": v(1007.54, 812.8) * mm, "end": v(1007.54, 716.28) * mm});
            skLineSegment(sketch, "E3.3.9.1", {"start": v(911.02, 812.8) * mm, "end": v(1007.54, 812.8) * mm});
            skLineSegment(sketch, "E3.6.9.1", {"start": v(911.02, 812.8) * mm, "end": v(911.02, 716.28) * mm});
            skLineSegment(sketch, "E3.9.9.1", {"start": v(911.02, 716.28) * mm, "end": v(1007.54, 716.28) * mm});
            skLineSegment(sketch, "E3.0.9.2", {"start": v(1007.54, 711.2) * mm, "end": v(1007.54, 614.68) * mm});
            skLineSegment(sketch, "E3.3.9.2", {"start": v(911.02, 711.2) * mm, "end": v(1007.54, 711.2) * mm});
            skLineSegment(sketch, "E3.6.9.2", {"start": v(911.02, 711.2) * mm, "end": v(911.02, 614.68) * mm});
            skLineSegment(sketch, "E3.9.9.2", {"start": v(911.02, 614.68) * mm, "end": v(1007.54, 614.68) * mm});
            skLineSegment(sketch, "E3.0.9.3", {"start": v(1007.54, 609.6) * mm, "end": v(1007.54, 513.08) * mm});
            skLineSegment(sketch, "E3.3.9.3", {"start": v(911.02, 609.6) * mm, "end": v(1007.54, 609.6) * mm});
            skLineSegment(sketch, "E3.6.9.3", {"start": v(911.02, 609.6) * mm, "end": v(911.02, 513.08) * mm});
            skLineSegment(sketch, "E3.9.9.3", {"start": v(911.02, 513.08) * mm, "end": v(1007.54, 513.08) * mm});
            skLineSegment(sketch, "E3.0.9.4", {"start": v(1007.54, 508) * mm, "end": v(1007.54, 411.48) * mm});
            skLineSegment(sketch, "E3.3.9.4", {"start": v(911.02, 508) * mm, "end": v(1007.54, 508) * mm});
            skLineSegment(sketch, "E3.6.9.4", {"start": v(911.02, 508) * mm, "end": v(911.02, 411.48) * mm});
            skLineSegment(sketch, "E3.9.9.4", {"start": v(911.02, 411.48) * mm, "end": v(1007.54, 411.48) * mm});
            skLineSegment(sketch, "E3.0.9.5", {"start": v(1007.54, 406.4) * mm, "end": v(1007.54, 309.88) * mm});
            skLineSegment(sketch, "E3.3.9.5", {"start": v(911.02, 406.4) * mm, "end": v(1007.54, 406.4) * mm});
            skLineSegment(sketch, "E3.6.9.5", {"start": v(911.02, 406.4) * mm, "end": v(911.02, 309.88) * mm});
            skLineSegment(sketch, "E3.9.9.5", {"start": v(911.02, 309.88) * mm, "end": v(1007.54, 309.88) * mm});
            skLineSegment(sketch, "E3.0.9.6", {"start": v(1007.54, 304.8) * mm, "end": v(1007.54, 208.28) * mm});
            skLineSegment(sketch, "E3.3.9.6", {"start": v(911.02, 304.8) * mm, "end": v(1007.54, 304.8) * mm});
            skLineSegment(sketch, "E3.6.9.6", {"start": v(911.02, 304.8) * mm, "end": v(911.02, 208.28) * mm});
            skLineSegment(sketch, "E3.9.9.6", {"start": v(911.02, 208.28) * mm, "end": v(1007.54, 208.28) * mm});
            skLineSegment(sketch, "E3.0.9.7", {"start": v(1007.54, 203.2) * mm, "end": v(1007.54, 106.68) * mm});
            skLineSegment(sketch, "E3.3.9.7", {"start": v(911.02, 203.2) * mm, "end": v(1007.54, 203.2) * mm});
            skLineSegment(sketch, "E3.6.9.7", {"start": v(911.02, 203.2) * mm, "end": v(911.02, 106.68) * mm});
            skLineSegment(sketch, "E3.9.9.7", {"start": v(911.02, 106.68) * mm, "end": v(1007.54, 106.68) * mm});
            skLineSegment(sketch, "E3.0.9.8", {"start": v(1007.54, 101.6) * mm, "end": v(1007.54, 5.08) * mm});
            skLineSegment(sketch, "E3.3.9.8", {"start": v(911.02, 101.6) * mm, "end": v(1007.54, 101.6) * mm});
            skLineSegment(sketch, "E3.6.9.8", {"start": v(911.02, 101.6) * mm, "end": v(911.02, 5.08) * mm});
            skLineSegment(sketch, "E3.9.9.8", {"start": v(911.02, 5.08) * mm, "end": v(1007.54, 5.08) * mm});
            skLineSegment(sketch, "E3.0.10.0", {"start": v(1108.2, 914.4) * mm, "end": v(1108.2, 817.88) * mm});
            skLineSegment(sketch, "E3.3.10.0", {"start": v(1011.68, 914.4) * mm, "end": v(1108.2, 914.4) * mm});
            skLineSegment(sketch, "E3.6.10.0", {"start": v(1011.68, 914.4) * mm, "end": v(1011.68, 817.88) * mm});
            skLineSegment(sketch, "E3.9.10.0", {"start": v(1011.68, 817.88) * mm, "end": v(1108.2, 817.88) * mm});
            skLineSegment(sketch, "E3.0.10.1", {"start": v(1108.2, 812.8) * mm, "end": v(1108.2, 716.28) * mm});
            skLineSegment(sketch, "E3.3.10.1", {"start": v(1011.68, 812.8) * mm, "end": v(1108.2, 812.8) * mm});
            skLineSegment(sketch, "E3.6.10.1", {"start": v(1011.68, 812.8) * mm, "end": v(1011.68, 716.28) * mm});
            skLineSegment(sketch, "E3.9.10.1", {"start": v(1011.68, 716.28) * mm, "end": v(1108.2, 716.28) * mm});
            skLineSegment(sketch, "E3.0.10.2", {"start": v(1108.2, 711.2) * mm, "end": v(1108.2, 614.68) * mm});
            skLineSegment(sketch, "E3.3.10.2", {"start": v(1011.68, 711.2) * mm, "end": v(1108.2, 711.2) * mm});
            skLineSegment(sketch, "E3.6.10.2", {"start": v(1011.68, 711.2) * mm, "end": v(1011.68, 614.68) * mm});
            skLineSegment(sketch, "E3.9.10.2", {"start": v(1011.68, 614.68) * mm, "end": v(1108.2, 614.68) * mm});
            skLineSegment(sketch, "E3.0.10.3", {"start": v(1108.2, 609.6) * mm, "end": v(1108.2, 513.08) * mm});
            skLineSegment(sketch, "E3.3.10.3", {"start": v(1011.68, 609.6) * mm, "end": v(1108.2, 609.6) * mm});
            skLineSegment(sketch, "E3.6.10.3", {"start": v(1011.68, 609.6) * mm, "end": v(1011.68, 513.08) * mm});
            skLineSegment(sketch, "E3.9.10.3", {"start": v(1011.68, 513.08) * mm, "end": v(1108.2, 513.08) * mm});
            skLineSegment(sketch, "E3.0.10.4", {"start": v(1108.2, 508) * mm, "end": v(1108.2, 411.48) * mm});
            skLineSegment(sketch, "E3.3.10.4", {"start": v(1011.68, 508) * mm, "end": v(1108.2, 508) * mm});
            skLineSegment(sketch, "E3.6.10.4", {"start": v(1011.68, 508) * mm, "end": v(1011.68, 411.48) * mm});
            skLineSegment(sketch, "E3.9.10.4", {"start": v(1011.68, 411.48) * mm, "end": v(1108.2, 411.48) * mm});
            skLineSegment(sketch, "E3.0.10.5", {"start": v(1108.2, 406.4) * mm, "end": v(1108.2, 309.88) * mm});
            skLineSegment(sketch, "E3.3.10.5", {"start": v(1011.68, 406.4) * mm, "end": v(1108.2, 406.4) * mm});
            skLineSegment(sketch, "E3.6.10.5", {"start": v(1011.68, 406.4) * mm, "end": v(1011.68, 309.88) * mm});
            skLineSegment(sketch, "E3.9.10.5", {"start": v(1011.68, 309.88) * mm, "end": v(1108.2, 309.88) * mm});
            skLineSegment(sketch, "E3.0.10.6", {"start": v(1108.2, 304.8) * mm, "end": v(1108.2, 208.28) * mm});
            skLineSegment(sketch, "E3.3.10.6", {"start": v(1011.68, 304.8) * mm, "end": v(1108.2, 304.8) * mm});
            skLineSegment(sketch, "E3.6.10.6", {"start": v(1011.68, 304.8) * mm, "end": v(1011.68, 208.28) * mm});
            skLineSegment(sketch, "E3.9.10.6", {"start": v(1011.68, 208.28) * mm, "end": v(1108.2, 208.28) * mm});
            skLineSegment(sketch, "E3.0.10.7", {"start": v(1108.2, 203.2) * mm, "end": v(1108.2, 106.68) * mm});
            skLineSegment(sketch, "E3.3.10.7", {"start": v(1011.68, 203.2) * mm, "end": v(1108.2, 203.2) * mm});
            skLineSegment(sketch, "E3.6.10.7", {"start": v(1011.68, 203.2) * mm, "end": v(1011.68, 106.68) * mm});
            skLineSegment(sketch, "E3.9.10.7", {"start": v(1011.68, 106.68) * mm, "end": v(1108.2, 106.68) * mm});
            skLineSegment(sketch, "E3.0.10.8", {"start": v(1108.2, 101.6) * mm, "end": v(1108.2, 5.08) * mm});
            skLineSegment(sketch, "E3.3.10.8", {"start": v(1011.68, 101.6) * mm, "end": v(1108.2, 101.6) * mm});
            skLineSegment(sketch, "E3.6.10.8", {"start": v(1011.68, 101.6) * mm, "end": v(1011.68, 5.08) * mm});
            skLineSegment(sketch, "E3.9.10.8", {"start": v(1011.68, 5.08) * mm, "end": v(1108.2, 5.08) * mm});
            skLineSegment(sketch, "E3.0.11.0", {"start": v(1208.86, 914.4) * mm, "end": v(1208.86, 817.88) * mm});
            skLineSegment(sketch, "E3.3.11.0", {"start": v(1112.34, 914.4) * mm, "end": v(1208.86, 914.4) * mm});
            skLineSegment(sketch, "E3.6.11.0", {"start": v(1112.34, 914.4) * mm, "end": v(1112.34, 817.88) * mm});
            skLineSegment(sketch, "E3.9.11.0", {"start": v(1112.34, 817.88) * mm, "end": v(1208.86, 817.88) * mm});
            skLineSegment(sketch, "E3.0.11.1", {"start": v(1208.86, 812.8) * mm, "end": v(1208.86, 716.28) * mm});
            skLineSegment(sketch, "E3.3.11.1", {"start": v(1112.34, 812.8) * mm, "end": v(1208.86, 812.8) * mm});
            skLineSegment(sketch, "E3.6.11.1", {"start": v(1112.34, 812.8) * mm, "end": v(1112.34, 716.28) * mm});
            skLineSegment(sketch, "E3.9.11.1", {"start": v(1112.34, 716.28) * mm, "end": v(1208.86, 716.28) * mm});
            skLineSegment(sketch, "E3.0.11.2", {"start": v(1208.86, 711.2) * mm, "end": v(1208.86, 614.68) * mm});
            skLineSegment(sketch, "E3.3.11.2", {"start": v(1112.34, 711.2) * mm, "end": v(1208.86, 711.2) * mm});
            skLineSegment(sketch, "E3.6.11.2", {"start": v(1112.34, 711.2) * mm, "end": v(1112.34, 614.68) * mm});
            skLineSegment(sketch, "E3.9.11.2", {"start": v(1112.34, 614.68) * mm, "end": v(1208.86, 614.68) * mm});
            skLineSegment(sketch, "E3.0.11.3", {"start": v(1208.86, 609.6) * mm, "end": v(1208.86, 513.08) * mm});
            skLineSegment(sketch, "E3.3.11.3", {"start": v(1112.34, 609.6) * mm, "end": v(1208.86, 609.6) * mm});
            skLineSegment(sketch, "E3.6.11.3", {"start": v(1112.34, 609.6) * mm, "end": v(1112.34, 513.08) * mm});
            skLineSegment(sketch, "E3.9.11.3", {"start": v(1112.34, 513.08) * mm, "end": v(1208.86, 513.08) * mm});
            skLineSegment(sketch, "E3.0.11.4", {"start": v(1208.86, 508) * mm, "end": v(1208.86, 411.48) * mm});
            skLineSegment(sketch, "E3.3.11.4", {"start": v(1112.34, 508) * mm, "end": v(1208.86, 508) * mm});
            skLineSegment(sketch, "E3.6.11.4", {"start": v(1112.34, 508) * mm, "end": v(1112.34, 411.48) * mm});
            skLineSegment(sketch, "E3.9.11.4", {"start": v(1112.34, 411.48) * mm, "end": v(1208.86, 411.48) * mm});
            skLineSegment(sketch, "E3.0.11.5", {"start": v(1208.86, 406.4) * mm, "end": v(1208.86, 309.88) * mm});
            skLineSegment(sketch, "E3.3.11.5", {"start": v(1112.34, 406.4) * mm, "end": v(1208.86, 406.4) * mm});
            skLineSegment(sketch, "E3.6.11.5", {"start": v(1112.34, 406.4) * mm, "end": v(1112.34, 309.88) * mm});
            skLineSegment(sketch, "E3.9.11.5", {"start": v(1112.34, 309.88) * mm, "end": v(1208.86, 309.88) * mm});
            skLineSegment(sketch, "E3.0.11.6", {"start": v(1208.86, 304.8) * mm, "end": v(1208.86, 208.28) * mm});
            skLineSegment(sketch, "E3.3.11.6", {"start": v(1112.34, 304.8) * mm, "end": v(1208.86, 304.8) * mm});
            skLineSegment(sketch, "E3.6.11.6", {"start": v(1112.34, 304.8) * mm, "end": v(1112.34, 208.28) * mm});
            skLineSegment(sketch, "E3.9.11.6", {"start": v(1112.34, 208.28) * mm, "end": v(1208.86, 208.28) * mm});
            skLineSegment(sketch, "E3.0.11.7", {"start": v(1208.86, 203.2) * mm, "end": v(1208.86, 106.68) * mm});
            skLineSegment(sketch, "E3.3.11.7", {"start": v(1112.34, 203.2) * mm, "end": v(1208.86, 203.2) * mm});
            skLineSegment(sketch, "E3.6.11.7", {"start": v(1112.34, 203.2) * mm, "end": v(1112.34, 106.68) * mm});
            skLineSegment(sketch, "E3.9.11.7", {"start": v(1112.34, 106.68) * mm, "end": v(1208.86, 106.68) * mm});
            skLineSegment(sketch, "E3.0.11.8", {"start": v(1208.86, 101.6) * mm, "end": v(1208.86, 5.08) * mm});
            skLineSegment(sketch, "E3.3.11.8", {"start": v(1112.34, 101.6) * mm, "end": v(1208.86, 101.6) * mm});
            skLineSegment(sketch, "E3.6.11.8", {"start": v(1112.34, 101.6) * mm, "end": v(1112.34, 5.08) * mm});
            skLineSegment(sketch, "E3.9.11.8", {"start": v(1112.34, 5.08) * mm, "end": v(1208.86, 5.08) * mm});
            skLineSegment(sketch, "E3.0.12.0", {"start": v(1309.52, 914.4) * mm, "end": v(1309.52, 817.88) * mm});
            skLineSegment(sketch, "E3.3.12.0", {"start": v(1213, 914.4) * mm, "end": v(1309.52, 914.4) * mm});
            skLineSegment(sketch, "E3.6.12.0", {"start": v(1213, 914.4) * mm, "end": v(1213, 817.88) * mm});
            skLineSegment(sketch, "E3.9.12.0", {"start": v(1213, 817.88) * mm, "end": v(1309.52, 817.88) * mm});
            skLineSegment(sketch, "E3.0.12.1", {"start": v(1309.52, 812.8) * mm, "end": v(1309.52, 716.28) * mm});
            skLineSegment(sketch, "E3.3.12.1", {"start": v(1213, 812.8) * mm, "end": v(1309.52, 812.8) * mm});
            skLineSegment(sketch, "E3.6.12.1", {"start": v(1213, 812.8) * mm, "end": v(1213, 716.28) * mm});
            skLineSegment(sketch, "E3.9.12.1", {"start": v(1213, 716.28) * mm, "end": v(1309.52, 716.28) * mm});
            skLineSegment(sketch, "E3.0.12.2", {"start": v(1309.52, 711.2) * mm, "end": v(1309.52, 614.68) * mm});
            skLineSegment(sketch, "E3.3.12.2", {"start": v(1213, 711.2) * mm, "end": v(1309.52, 711.2) * mm});
            skLineSegment(sketch, "E3.6.12.2", {"start": v(1213, 711.2) * mm, "end": v(1213, 614.68) * mm});
            skLineSegment(sketch, "E3.9.12.2", {"start": v(1213, 614.68) * mm, "end": v(1309.52, 614.68) * mm});
            skLineSegment(sketch, "E3.0.12.3", {"start": v(1309.52, 609.6) * mm, "end": v(1309.52, 513.08) * mm});
            skLineSegment(sketch, "E3.3.12.3", {"start": v(1213, 609.6) * mm, "end": v(1309.52, 609.6) * mm});
            skLineSegment(sketch, "E3.6.12.3", {"start": v(1213, 609.6) * mm, "end": v(1213, 513.08) * mm});
            skLineSegment(sketch, "E3.9.12.3", {"start": v(1213, 513.08) * mm, "end": v(1309.52, 513.08) * mm});
            skLineSegment(sketch, "E3.0.12.4", {"start": v(1309.52, 508) * mm, "end": v(1309.52, 411.48) * mm});
            skLineSegment(sketch, "E3.3.12.4", {"start": v(1213, 508) * mm, "end": v(1309.52, 508) * mm});
            skLineSegment(sketch, "E3.6.12.4", {"start": v(1213, 508) * mm, "end": v(1213, 411.48) * mm});
            skLineSegment(sketch, "E3.9.12.4", {"start": v(1213, 411.48) * mm, "end": v(1309.52, 411.48) * mm});
            skLineSegment(sketch, "E3.0.12.5", {"start": v(1309.52, 406.4) * mm, "end": v(1309.52, 309.88) * mm});
            skLineSegment(sketch, "E3.3.12.5", {"start": v(1213, 406.4) * mm, "end": v(1309.52, 406.4) * mm});
            skLineSegment(sketch, "E3.6.12.5", {"start": v(1213, 406.4) * mm, "end": v(1213, 309.88) * mm});
            skLineSegment(sketch, "E3.9.12.5", {"start": v(1213, 309.88) * mm, "end": v(1309.52, 309.88) * mm});
            skLineSegment(sketch, "E3.0.12.6", {"start": v(1309.52, 304.8) * mm, "end": v(1309.52, 208.28) * mm});
            skLineSegment(sketch, "E3.3.12.6", {"start": v(1213, 304.8) * mm, "end": v(1309.52, 304.8) * mm});
            skLineSegment(sketch, "E3.6.12.6", {"start": v(1213, 304.8) * mm, "end": v(1213, 208.28) * mm});
            skLineSegment(sketch, "E3.9.12.6", {"start": v(1213, 208.28) * mm, "end": v(1309.52, 208.28) * mm});
            skLineSegment(sketch, "E3.0.12.7", {"start": v(1309.52, 203.2) * mm, "end": v(1309.52, 106.68) * mm});
            skLineSegment(sketch, "E3.3.12.7", {"start": v(1213, 203.2) * mm, "end": v(1309.52, 203.2) * mm});
            skLineSegment(sketch, "E3.6.12.7", {"start": v(1213, 203.2) * mm, "end": v(1213, 106.68) * mm});
            skLineSegment(sketch, "E3.9.12.7", {"start": v(1213, 106.68) * mm, "end": v(1309.52, 106.68) * mm});
            skLineSegment(sketch, "E3.0.12.8", {"start": v(1309.52, 101.6) * mm, "end": v(1309.52, 5.08) * mm});
            skLineSegment(sketch, "E3.3.12.8", {"start": v(1213, 101.6) * mm, "end": v(1309.52, 101.6) * mm});
            skLineSegment(sketch, "E3.6.12.8", {"start": v(1213, 101.6) * mm, "end": v(1213, 5.08) * mm});
            skLineSegment(sketch, "E3.9.12.8", {"start": v(1213, 5.08) * mm, "end": v(1309.52, 5.08) * mm});
            skLineSegment(sketch, "E3.0.13.0", {"start": v(1410.18, 914.4) * mm, "end": v(1410.18, 817.88) * mm});
            skLineSegment(sketch, "E3.3.13.0", {"start": v(1313.66, 914.4) * mm, "end": v(1410.18, 914.4) * mm});
            skLineSegment(sketch, "E3.6.13.0", {"start": v(1313.66, 914.4) * mm, "end": v(1313.66, 817.88) * mm});
            skLineSegment(sketch, "E3.9.13.0", {"start": v(1313.66, 817.88) * mm, "end": v(1410.18, 817.88) * mm});
            skLineSegment(sketch, "E3.0.13.1", {"start": v(1410.18, 812.8) * mm, "end": v(1410.18, 716.28) * mm});
            skLineSegment(sketch, "E3.3.13.1", {"start": v(1313.66, 812.8) * mm, "end": v(1410.18, 812.8) * mm});
            skLineSegment(sketch, "E3.6.13.1", {"start": v(1313.66, 812.8) * mm, "end": v(1313.66, 716.28) * mm});
            skLineSegment(sketch, "E3.9.13.1", {"start": v(1313.66, 716.28) * mm, "end": v(1410.18, 716.28) * mm});
            skLineSegment(sketch, "E3.0.13.2", {"start": v(1410.18, 711.2) * mm, "end": v(1410.18, 614.68) * mm});
            skLineSegment(sketch, "E3.3.13.2", {"start": v(1313.66, 711.2) * mm, "end": v(1410.18, 711.2) * mm});
            skLineSegment(sketch, "E3.6.13.2", {"start": v(1313.66, 711.2) * mm, "end": v(1313.66, 614.68) * mm});
            skLineSegment(sketch, "E3.9.13.2", {"start": v(1313.66, 614.68) * mm, "end": v(1410.18, 614.68) * mm});
            skLineSegment(sketch, "E3.0.13.3", {"start": v(1410.18, 609.6) * mm, "end": v(1410.18, 513.08) * mm});
            skLineSegment(sketch, "E3.3.13.3", {"start": v(1313.66, 609.6) * mm, "end": v(1410.18, 609.6) * mm});
            skLineSegment(sketch, "E3.6.13.3", {"start": v(1313.66, 609.6) * mm, "end": v(1313.66, 513.08) * mm});
            skLineSegment(sketch, "E3.9.13.3", {"start": v(1313.66, 513.08) * mm, "end": v(1410.18, 513.08) * mm});
            skLineSegment(sketch, "E3.0.13.4", {"start": v(1410.18, 508) * mm, "end": v(1410.18, 411.48) * mm});
            skLineSegment(sketch, "E3.3.13.4", {"start": v(1313.66, 508) * mm, "end": v(1410.18, 508) * mm});
            skLineSegment(sketch, "E3.6.13.4", {"start": v(1313.66, 508) * mm, "end": v(1313.66, 411.48) * mm});
            skLineSegment(sketch, "E3.9.13.4", {"start": v(1313.66, 411.48) * mm, "end": v(1410.18, 411.48) * mm});
            skLineSegment(sketch, "E3.0.13.5", {"start": v(1410.18, 406.4) * mm, "end": v(1410.18, 309.88) * mm});
            skLineSegment(sketch, "E3.3.13.5", {"start": v(1313.66, 406.4) * mm, "end": v(1410.18, 406.4) * mm});
            skLineSegment(sketch, "E3.6.13.5", {"start": v(1313.66, 406.4) * mm, "end": v(1313.66, 309.88) * mm});
            skLineSegment(sketch, "E3.9.13.5", {"start": v(1313.66, 309.88) * mm, "end": v(1410.18, 309.88) * mm});
            skLineSegment(sketch, "E3.0.13.6", {"start": v(1410.18, 304.8) * mm, "end": v(1410.18, 208.28) * mm});
            skLineSegment(sketch, "E3.3.13.6", {"start": v(1313.66, 304.8) * mm, "end": v(1410.18, 304.8) * mm});
            skLineSegment(sketch, "E3.6.13.6", {"start": v(1313.66, 304.8) * mm, "end": v(1313.66, 208.28) * mm});
            skLineSegment(sketch, "E3.9.13.6", {"start": v(1313.66, 208.28) * mm, "end": v(1410.18, 208.28) * mm});
            skLineSegment(sketch, "E3.0.13.7", {"start": v(1410.18, 203.2) * mm, "end": v(1410.18, 106.68) * mm});
            skLineSegment(sketch, "E3.3.13.7", {"start": v(1313.66, 203.2) * mm, "end": v(1410.18, 203.2) * mm});
            skLineSegment(sketch, "E3.6.13.7", {"start": v(1313.66, 203.2) * mm, "end": v(1313.66, 106.68) * mm});
            skLineSegment(sketch, "E3.9.13.7", {"start": v(1313.66, 106.68) * mm, "end": v(1410.18, 106.68) * mm});
            skLineSegment(sketch, "E3.0.13.8", {"start": v(1410.18, 101.6) * mm, "end": v(1410.18, 5.08) * mm});
            skLineSegment(sketch, "E3.3.13.8", {"start": v(1313.66, 101.6) * mm, "end": v(1410.18, 101.6) * mm});
            skLineSegment(sketch, "E3.6.13.8", {"start": v(1313.66, 101.6) * mm, "end": v(1313.66, 5.08) * mm});
            skLineSegment(sketch, "E3.9.13.8", {"start": v(1313.66, 5.08) * mm, "end": v(1410.18, 5.08) * mm});
            skLineSegment(sketch, "E3.0.14.0", {"start": v(1510.84, 914.4) * mm, "end": v(1510.84, 817.88) * mm});
            skLineSegment(sketch, "E3.3.14.0", {"start": v(1414.32, 914.4) * mm, "end": v(1510.84, 914.4) * mm});
            skLineSegment(sketch, "E3.6.14.0", {"start": v(1414.32, 914.4) * mm, "end": v(1414.32, 817.88) * mm});
            skLineSegment(sketch, "E3.9.14.0", {"start": v(1414.32, 817.88) * mm, "end": v(1510.84, 817.88) * mm});
            skLineSegment(sketch, "E3.0.14.1", {"start": v(1510.84, 812.8) * mm, "end": v(1510.84, 716.28) * mm});
            skLineSegment(sketch, "E3.3.14.1", {"start": v(1414.32, 812.8) * mm, "end": v(1510.84, 812.8) * mm});
            skLineSegment(sketch, "E3.6.14.1", {"start": v(1414.32, 812.8) * mm, "end": v(1414.32, 716.28) * mm});
            skLineSegment(sketch, "E3.9.14.1", {"start": v(1414.32, 716.28) * mm, "end": v(1510.84, 716.28) * mm});
            skLineSegment(sketch, "E3.0.14.2", {"start": v(1510.84, 711.2) * mm, "end": v(1510.84, 614.68) * mm});
            skLineSegment(sketch, "E3.3.14.2", {"start": v(1414.32, 711.2) * mm, "end": v(1510.84, 711.2) * mm});
            skLineSegment(sketch, "E3.6.14.2", {"start": v(1414.32, 711.2) * mm, "end": v(1414.32, 614.68) * mm});
            skLineSegment(sketch, "E3.9.14.2", {"start": v(1414.32, 614.68) * mm, "end": v(1510.84, 614.68) * mm});
            skLineSegment(sketch, "E3.0.14.3", {"start": v(1510.84, 609.6) * mm, "end": v(1510.84, 513.08) * mm});
            skLineSegment(sketch, "E3.3.14.3", {"start": v(1414.32, 609.6) * mm, "end": v(1510.84, 609.6) * mm});
            skLineSegment(sketch, "E3.6.14.3", {"start": v(1414.32, 609.6) * mm, "end": v(1414.32, 513.08) * mm});
            skLineSegment(sketch, "E3.9.14.3", {"start": v(1414.32, 513.08) * mm, "end": v(1510.84, 513.08) * mm});
            skLineSegment(sketch, "E3.0.14.4", {"start": v(1510.84, 508) * mm, "end": v(1510.84, 411.48) * mm});
            skLineSegment(sketch, "E3.3.14.4", {"start": v(1414.32, 508) * mm, "end": v(1510.84, 508) * mm});
            skLineSegment(sketch, "E3.6.14.4", {"start": v(1414.32, 508) * mm, "end": v(1414.32, 411.48) * mm});
            skLineSegment(sketch, "E3.9.14.4", {"start": v(1414.32, 411.48) * mm, "end": v(1510.84, 411.48) * mm});
            skLineSegment(sketch, "E3.0.14.5", {"start": v(1510.84, 406.4) * mm, "end": v(1510.84, 309.88) * mm});
            skLineSegment(sketch, "E3.3.14.5", {"start": v(1414.32, 406.4) * mm, "end": v(1510.84, 406.4) * mm});
            skLineSegment(sketch, "E3.6.14.5", {"start": v(1414.32, 406.4) * mm, "end": v(1414.32, 309.88) * mm});
            skLineSegment(sketch, "E3.9.14.5", {"start": v(1414.32, 309.88) * mm, "end": v(1510.84, 309.88) * mm});
            skLineSegment(sketch, "E3.0.14.6", {"start": v(1510.84, 304.8) * mm, "end": v(1510.84, 208.28) * mm});
            skLineSegment(sketch, "E3.3.14.6", {"start": v(1414.32, 304.8) * mm, "end": v(1510.84, 304.8) * mm});
            skLineSegment(sketch, "E3.6.14.6", {"start": v(1414.32, 304.8) * mm, "end": v(1414.32, 208.28) * mm});
            skLineSegment(sketch, "E3.9.14.6", {"start": v(1414.32, 208.28) * mm, "end": v(1510.84, 208.28) * mm});
            skLineSegment(sketch, "E3.0.14.7", {"start": v(1510.84, 203.2) * mm, "end": v(1510.84, 106.68) * mm});
            skLineSegment(sketch, "E3.3.14.7", {"start": v(1414.32, 203.2) * mm, "end": v(1510.84, 203.2) * mm});
            skLineSegment(sketch, "E3.6.14.7", {"start": v(1414.32, 203.2) * mm, "end": v(1414.32, 106.68) * mm});
            skLineSegment(sketch, "E3.9.14.7", {"start": v(1414.32, 106.68) * mm, "end": v(1510.84, 106.68) * mm});
            skLineSegment(sketch, "E3.0.14.8", {"start": v(1510.84, 101.6) * mm, "end": v(1510.84, 5.08) * mm});
            skLineSegment(sketch, "E3.3.14.8", {"start": v(1414.32, 101.6) * mm, "end": v(1510.84, 101.6) * mm});
            skLineSegment(sketch, "E3.6.14.8", {"start": v(1414.32, 101.6) * mm, "end": v(1414.32, 5.08) * mm});
            skLineSegment(sketch, "E3.9.14.8", {"start": v(1414.32, 5.08) * mm, "end": v(1510.84, 5.08) * mm});
            skLineSegment(sketch, "E3.0.15.0", {"start": v(1611.5, 914.4) * mm, "end": v(1611.5, 817.88) * mm});
            skLineSegment(sketch, "E3.3.15.0", {"start": v(1514.98, 914.4) * mm, "end": v(1611.5, 914.4) * mm});
            skLineSegment(sketch, "E3.6.15.0", {"start": v(1514.98, 914.4) * mm, "end": v(1514.98, 817.88) * mm});
            skLineSegment(sketch, "E3.9.15.0", {"start": v(1514.98, 817.88) * mm, "end": v(1611.5, 817.88) * mm});
            skLineSegment(sketch, "E3.0.15.1", {"start": v(1611.5, 812.8) * mm, "end": v(1611.5, 716.28) * mm});
            skLineSegment(sketch, "E3.3.15.1", {"start": v(1514.98, 812.8) * mm, "end": v(1611.5, 812.8) * mm});
            skLineSegment(sketch, "E3.6.15.1", {"start": v(1514.98, 812.8) * mm, "end": v(1514.98, 716.28) * mm});
            skLineSegment(sketch, "E3.9.15.1", {"start": v(1514.98, 716.28) * mm, "end": v(1611.5, 716.28) * mm});
            skLineSegment(sketch, "E3.0.15.2", {"start": v(1611.5, 711.2) * mm, "end": v(1611.5, 614.68) * mm});
            skLineSegment(sketch, "E3.3.15.2", {"start": v(1514.98, 711.2) * mm, "end": v(1611.5, 711.2) * mm});
            skLineSegment(sketch, "E3.6.15.2", {"start": v(1514.98, 711.2) * mm, "end": v(1514.98, 614.68) * mm});
            skLineSegment(sketch, "E3.9.15.2", {"start": v(1514.98, 614.68) * mm, "end": v(1611.5, 614.68) * mm});
            skLineSegment(sketch, "E3.0.15.3", {"start": v(1611.5, 609.6) * mm, "end": v(1611.5, 513.08) * mm});
            skLineSegment(sketch, "E3.3.15.3", {"start": v(1514.98, 609.6) * mm, "end": v(1611.5, 609.6) * mm});
            skLineSegment(sketch, "E3.6.15.3", {"start": v(1514.98, 609.6) * mm, "end": v(1514.98, 513.08) * mm});
            skLineSegment(sketch, "E3.9.15.3", {"start": v(1514.98, 513.08) * mm, "end": v(1611.5, 513.08) * mm});
            skLineSegment(sketch, "E3.0.15.4", {"start": v(1611.5, 508) * mm, "end": v(1611.5, 411.48) * mm});
            skLineSegment(sketch, "E3.3.15.4", {"start": v(1514.98, 508) * mm, "end": v(1611.5, 508) * mm});
            skLineSegment(sketch, "E3.6.15.4", {"start": v(1514.98, 508) * mm, "end": v(1514.98, 411.48) * mm});
            skLineSegment(sketch, "E3.9.15.4", {"start": v(1514.98, 411.48) * mm, "end": v(1611.5, 411.48) * mm});
            skLineSegment(sketch, "E3.0.15.5", {"start": v(1611.5, 406.4) * mm, "end": v(1611.5, 309.88) * mm});
            skLineSegment(sketch, "E3.3.15.5", {"start": v(1514.98, 406.4) * mm, "end": v(1611.5, 406.4) * mm});
            skLineSegment(sketch, "E3.6.15.5", {"start": v(1514.98, 406.4) * mm, "end": v(1514.98, 309.88) * mm});
            skLineSegment(sketch, "E3.9.15.5", {"start": v(1514.98, 309.88) * mm, "end": v(1611.5, 309.88) * mm});
            skLineSegment(sketch, "E3.0.15.6", {"start": v(1611.5, 304.8) * mm, "end": v(1611.5, 208.28) * mm});
            skLineSegment(sketch, "E3.3.15.6", {"start": v(1514.98, 304.8) * mm, "end": v(1611.5, 304.8) * mm});
            skLineSegment(sketch, "E3.6.15.6", {"start": v(1514.98, 304.8) * mm, "end": v(1514.98, 208.28) * mm});
            skLineSegment(sketch, "E3.9.15.6", {"start": v(1514.98, 208.28) * mm, "end": v(1611.5, 208.28) * mm});
            skLineSegment(sketch, "E3.0.15.7", {"start": v(1611.5, 203.2) * mm, "end": v(1611.5, 106.68) * mm});
            skLineSegment(sketch, "E3.3.15.7", {"start": v(1514.98, 203.2) * mm, "end": v(1611.5, 203.2) * mm});
            skLineSegment(sketch, "E3.6.15.7", {"start": v(1514.98, 203.2) * mm, "end": v(1514.98, 106.68) * mm});
            skLineSegment(sketch, "E3.9.15.7", {"start": v(1514.98, 106.68) * mm, "end": v(1611.5, 106.68) * mm});
            skLineSegment(sketch, "E3.0.15.8", {"start": v(1611.5, 101.6) * mm, "end": v(1611.5, 5.08) * mm});
            skLineSegment(sketch, "E3.3.15.8", {"start": v(1514.98, 101.6) * mm, "end": v(1611.5, 101.6) * mm});
            skLineSegment(sketch, "E3.6.15.8", {"start": v(1514.98, 101.6) * mm, "end": v(1514.98, 5.08) * mm});
            skLineSegment(sketch, "E3.9.15.8", {"start": v(1514.98, 5.08) * mm, "end": v(1611.5, 5.08) * mm});
            skLineSegment(sketch, "E3.0.16.0", {"start": v(1712.16, 914.4) * mm, "end": v(1712.16, 817.88) * mm});
            skLineSegment(sketch, "E3.3.16.0", {"start": v(1615.64, 914.4) * mm, "end": v(1712.16, 914.4) * mm});
            skLineSegment(sketch, "E3.6.16.0", {"start": v(1615.64, 914.4) * mm, "end": v(1615.64, 817.88) * mm});
            skLineSegment(sketch, "E3.9.16.0", {"start": v(1615.64, 817.88) * mm, "end": v(1712.16, 817.88) * mm});
            skLineSegment(sketch, "E3.0.16.1", {"start": v(1712.16, 812.8) * mm, "end": v(1712.16, 716.28) * mm});
            skLineSegment(sketch, "E3.3.16.1", {"start": v(1615.64, 812.8) * mm, "end": v(1712.16, 812.8) * mm});
            skLineSegment(sketch, "E3.6.16.1", {"start": v(1615.64, 812.8) * mm, "end": v(1615.64, 716.28) * mm});
            skLineSegment(sketch, "E3.9.16.1", {"start": v(1615.64, 716.28) * mm, "end": v(1712.16, 716.28) * mm});
            skLineSegment(sketch, "E3.0.16.2", {"start": v(1712.16, 711.2) * mm, "end": v(1712.16, 614.68) * mm});
            skLineSegment(sketch, "E3.3.16.2", {"start": v(1615.64, 711.2) * mm, "end": v(1712.16, 711.2) * mm});
            skLineSegment(sketch, "E3.6.16.2", {"start": v(1615.64, 711.2) * mm, "end": v(1615.64, 614.68) * mm});
            skLineSegment(sketch, "E3.9.16.2", {"start": v(1615.64, 614.68) * mm, "end": v(1712.16, 614.68) * mm});
            skLineSegment(sketch, "E3.0.16.3", {"start": v(1712.16, 609.6) * mm, "end": v(1712.16, 513.08) * mm});
            skLineSegment(sketch, "E3.3.16.3", {"start": v(1615.64, 609.6) * mm, "end": v(1712.16, 609.6) * mm});
            skLineSegment(sketch, "E3.6.16.3", {"start": v(1615.64, 609.6) * mm, "end": v(1615.64, 513.08) * mm});
            skLineSegment(sketch, "E3.9.16.3", {"start": v(1615.64, 513.08) * mm, "end": v(1712.16, 513.08) * mm});
            skLineSegment(sketch, "E3.0.16.4", {"start": v(1712.16, 508) * mm, "end": v(1712.16, 411.48) * mm});
            skLineSegment(sketch, "E3.3.16.4", {"start": v(1615.64, 508) * mm, "end": v(1712.16, 508) * mm});
            skLineSegment(sketch, "E3.6.16.4", {"start": v(1615.64, 508) * mm, "end": v(1615.64, 411.48) * mm});
            skLineSegment(sketch, "E3.9.16.4", {"start": v(1615.64, 411.48) * mm, "end": v(1712.16, 411.48) * mm});
            skLineSegment(sketch, "E3.0.16.5", {"start": v(1712.16, 406.4) * mm, "end": v(1712.16, 309.88) * mm});
            skLineSegment(sketch, "E3.3.16.5", {"start": v(1615.64, 406.4) * mm, "end": v(1712.16, 406.4) * mm});
            skLineSegment(sketch, "E3.6.16.5", {"start": v(1615.64, 406.4) * mm, "end": v(1615.64, 309.88) * mm});
            skLineSegment(sketch, "E3.9.16.5", {"start": v(1615.64, 309.88) * mm, "end": v(1712.16, 309.88) * mm});
            skLineSegment(sketch, "E3.0.16.6", {"start": v(1712.16, 304.8) * mm, "end": v(1712.16, 208.28) * mm});
            skLineSegment(sketch, "E3.3.16.6", {"start": v(1615.64, 304.8) * mm, "end": v(1712.16, 304.8) * mm});
            skLineSegment(sketch, "E3.6.16.6", {"start": v(1615.64, 304.8) * mm, "end": v(1615.64, 208.28) * mm});
            skLineSegment(sketch, "E3.9.16.6", {"start": v(1615.64, 208.28) * mm, "end": v(1712.16, 208.28) * mm});
            skLineSegment(sketch, "E3.0.16.7", {"start": v(1712.16, 203.2) * mm, "end": v(1712.16, 106.68) * mm});
            skLineSegment(sketch, "E3.3.16.7", {"start": v(1615.64, 203.2) * mm, "end": v(1712.16, 203.2) * mm});
            skLineSegment(sketch, "E3.6.16.7", {"start": v(1615.64, 203.2) * mm, "end": v(1615.64, 106.68) * mm});
            skLineSegment(sketch, "E3.9.16.7", {"start": v(1615.64, 106.68) * mm, "end": v(1712.16, 106.68) * mm});
            skLineSegment(sketch, "E3.0.16.8", {"start": v(1712.16, 101.6) * mm, "end": v(1712.16, 5.08) * mm});
            skLineSegment(sketch, "E3.3.16.8", {"start": v(1615.64, 101.6) * mm, "end": v(1712.16, 101.6) * mm});
            skLineSegment(sketch, "E3.6.16.8", {"start": v(1615.64, 101.6) * mm, "end": v(1615.64, 5.08) * mm});
            skLineSegment(sketch, "E3.9.16.8", {"start": v(1615.64, 5.08) * mm, "end": v(1712.16, 5.08) * mm});
            skLineSegment(sketch, "E3.0.17.0", {"start": v(1812.82, 914.4) * mm, "end": v(1812.82, 817.88) * mm});
            skLineSegment(sketch, "E3.3.17.0", {"start": v(1716.3, 914.4) * mm, "end": v(1812.82, 914.4) * mm});
            skLineSegment(sketch, "E3.6.17.0", {"start": v(1716.3, 914.4) * mm, "end": v(1716.3, 817.88) * mm});
            skLineSegment(sketch, "E3.9.17.0", {"start": v(1716.3, 817.88) * mm, "end": v(1812.82, 817.88) * mm});
            skLineSegment(sketch, "E3.0.17.1", {"start": v(1812.82, 812.8) * mm, "end": v(1812.82, 716.28) * mm});
            skLineSegment(sketch, "E3.3.17.1", {"start": v(1716.3, 812.8) * mm, "end": v(1812.82, 812.8) * mm});
            skLineSegment(sketch, "E3.6.17.1", {"start": v(1716.3, 812.8) * mm, "end": v(1716.3, 716.28) * mm});
            skLineSegment(sketch, "E3.9.17.1", {"start": v(1716.3, 716.28) * mm, "end": v(1812.82, 716.28) * mm});
            skLineSegment(sketch, "E3.0.17.2", {"start": v(1812.82, 711.2) * mm, "end": v(1812.82, 614.68) * mm});
            skLineSegment(sketch, "E3.3.17.2", {"start": v(1716.3, 711.2) * mm, "end": v(1812.82, 711.2) * mm});
            skLineSegment(sketch, "E3.6.17.2", {"start": v(1716.3, 711.2) * mm, "end": v(1716.3, 614.68) * mm});
            skLineSegment(sketch, "E3.9.17.2", {"start": v(1716.3, 614.68) * mm, "end": v(1812.82, 614.68) * mm});
            skLineSegment(sketch, "E3.0.17.3", {"start": v(1812.82, 609.6) * mm, "end": v(1812.82, 513.08) * mm});
            skLineSegment(sketch, "E3.3.17.3", {"start": v(1716.3, 609.6) * mm, "end": v(1812.82, 609.6) * mm});
            skLineSegment(sketch, "E3.6.17.3", {"start": v(1716.3, 609.6) * mm, "end": v(1716.3, 513.08) * mm});
            skLineSegment(sketch, "E3.9.17.3", {"start": v(1716.3, 513.08) * mm, "end": v(1812.82, 513.08) * mm});
            skLineSegment(sketch, "E3.0.17.4", {"start": v(1812.82, 508) * mm, "end": v(1812.82, 411.48) * mm});
            skLineSegment(sketch, "E3.3.17.4", {"start": v(1716.3, 508) * mm, "end": v(1812.82, 508) * mm});
            skLineSegment(sketch, "E3.6.17.4", {"start": v(1716.3, 508) * mm, "end": v(1716.3, 411.48) * mm});
            skLineSegment(sketch, "E3.9.17.4", {"start": v(1716.3, 411.48) * mm, "end": v(1812.82, 411.48) * mm});
            skLineSegment(sketch, "E3.0.17.5", {"start": v(1812.82, 406.4) * mm, "end": v(1812.82, 309.88) * mm});
            skLineSegment(sketch, "E3.3.17.5", {"start": v(1716.3, 406.4) * mm, "end": v(1812.82, 406.4) * mm});
            skLineSegment(sketch, "E3.6.17.5", {"start": v(1716.3, 406.4) * mm, "end": v(1716.3, 309.88) * mm});
            skLineSegment(sketch, "E3.9.17.5", {"start": v(1716.3, 309.88) * mm, "end": v(1812.82, 309.88) * mm});
            skLineSegment(sketch, "E3.0.17.6", {"start": v(1812.82, 304.8) * mm, "end": v(1812.82, 208.28) * mm});
            skLineSegment(sketch, "E3.3.17.6", {"start": v(1716.3, 304.8) * mm, "end": v(1812.82, 304.8) * mm});
            skLineSegment(sketch, "E3.6.17.6", {"start": v(1716.3, 304.8) * mm, "end": v(1716.3, 208.28) * mm});
            skLineSegment(sketch, "E3.9.17.6", {"start": v(1716.3, 208.28) * mm, "end": v(1812.82, 208.28) * mm});
            skLineSegment(sketch, "E3.0.17.7", {"start": v(1812.82, 203.2) * mm, "end": v(1812.82, 106.68) * mm});
            skLineSegment(sketch, "E3.3.17.7", {"start": v(1716.3, 203.2) * mm, "end": v(1812.82, 203.2) * mm});
            skLineSegment(sketch, "E3.6.17.7", {"start": v(1716.3, 203.2) * mm, "end": v(1716.3, 106.68) * mm});
            skLineSegment(sketch, "E3.9.17.7", {"start": v(1716.3, 106.68) * mm, "end": v(1812.82, 106.68) * mm});
            skLineSegment(sketch, "E3.0.17.8", {"start": v(1812.82, 101.6) * mm, "end": v(1812.82, 5.08) * mm});
            skLineSegment(sketch, "E3.3.17.8", {"start": v(1716.3, 101.6) * mm, "end": v(1812.82, 101.6) * mm});
            skLineSegment(sketch, "E3.6.17.8", {"start": v(1716.3, 101.6) * mm, "end": v(1716.3, 5.08) * mm});
            skLineSegment(sketch, "E3.9.17.8", {"start": v(1716.3, 5.08) * mm, "end": v(1812.82, 5.08) * mm});
            skLineSegment(sketch, "E3.0.18.0", {"start": v(1913.48, 914.4) * mm, "end": v(1913.48, 817.88) * mm});
            skLineSegment(sketch, "E3.3.18.0", {"start": v(1816.96, 914.4) * mm, "end": v(1913.48, 914.4) * mm});
            skLineSegment(sketch, "E3.6.18.0", {"start": v(1816.96, 914.4) * mm, "end": v(1816.96, 817.88) * mm});
            skLineSegment(sketch, "E3.9.18.0", {"start": v(1816.96, 817.88) * mm, "end": v(1913.48, 817.88) * mm});
            skLineSegment(sketch, "E3.0.18.1", {"start": v(1913.48, 812.8) * mm, "end": v(1913.48, 716.28) * mm});
            skLineSegment(sketch, "E3.3.18.1", {"start": v(1816.96, 812.8) * mm, "end": v(1913.48, 812.8) * mm});
            skLineSegment(sketch, "E3.6.18.1", {"start": v(1816.96, 812.8) * mm, "end": v(1816.96, 716.28) * mm});
            skLineSegment(sketch, "E3.9.18.1", {"start": v(1816.96, 716.28) * mm, "end": v(1913.48, 716.28) * mm});
            skLineSegment(sketch, "E3.0.18.2", {"start": v(1913.48, 711.2) * mm, "end": v(1913.48, 614.68) * mm});
            skLineSegment(sketch, "E3.3.18.2", {"start": v(1816.96, 711.2) * mm, "end": v(1913.48, 711.2) * mm});
            skLineSegment(sketch, "E3.6.18.2", {"start": v(1816.96, 711.2) * mm, "end": v(1816.96, 614.68) * mm});
            skLineSegment(sketch, "E3.9.18.2", {"start": v(1816.96, 614.68) * mm, "end": v(1913.48, 614.68) * mm});
            skLineSegment(sketch, "E3.0.18.3", {"start": v(1913.48, 609.6) * mm, "end": v(1913.48, 513.08) * mm});
            skLineSegment(sketch, "E3.3.18.3", {"start": v(1816.96, 609.6) * mm, "end": v(1913.48, 609.6) * mm});
            skLineSegment(sketch, "E3.6.18.3", {"start": v(1816.96, 609.6) * mm, "end": v(1816.96, 513.08) * mm});
            skLineSegment(sketch, "E3.9.18.3", {"start": v(1816.96, 513.08) * mm, "end": v(1913.48, 513.08) * mm});
            skLineSegment(sketch, "E3.0.18.4", {"start": v(1913.48, 508) * mm, "end": v(1913.48, 411.48) * mm});
            skLineSegment(sketch, "E3.3.18.4", {"start": v(1816.96, 508) * mm, "end": v(1913.48, 508) * mm});
            skLineSegment(sketch, "E3.6.18.4", {"start": v(1816.96, 508) * mm, "end": v(1816.96, 411.48) * mm});
            skLineSegment(sketch, "E3.9.18.4", {"start": v(1816.96, 411.48) * mm, "end": v(1913.48, 411.48) * mm});
            skLineSegment(sketch, "E3.0.18.5", {"start": v(1913.48, 406.4) * mm, "end": v(1913.48, 309.88) * mm});
            skLineSegment(sketch, "E3.3.18.5", {"start": v(1816.96, 406.4) * mm, "end": v(1913.48, 406.4) * mm});
            skLineSegment(sketch, "E3.6.18.5", {"start": v(1816.96, 406.4) * mm, "end": v(1816.96, 309.88) * mm});
            skLineSegment(sketch, "E3.9.18.5", {"start": v(1816.96, 309.88) * mm, "end": v(1913.48, 309.88) * mm});
            skLineSegment(sketch, "E3.0.18.6", {"start": v(1913.48, 304.8) * mm, "end": v(1913.48, 208.28) * mm});
            skLineSegment(sketch, "E3.3.18.6", {"start": v(1816.96, 304.8) * mm, "end": v(1913.48, 304.8) * mm});
            skLineSegment(sketch, "E3.6.18.6", {"start": v(1816.96, 304.8) * mm, "end": v(1816.96, 208.28) * mm});
            skLineSegment(sketch, "E3.9.18.6", {"start": v(1816.96, 208.28) * mm, "end": v(1913.48, 208.28) * mm});
            skLineSegment(sketch, "E3.0.18.7", {"start": v(1913.48, 203.2) * mm, "end": v(1913.48, 106.68) * mm});
            skLineSegment(sketch, "E3.3.18.7", {"start": v(1816.96, 203.2) * mm, "end": v(1913.48, 203.2) * mm});
            skLineSegment(sketch, "E3.6.18.7", {"start": v(1816.96, 203.2) * mm, "end": v(1816.96, 106.68) * mm});
            skLineSegment(sketch, "E3.9.18.7", {"start": v(1816.96, 106.68) * mm, "end": v(1913.48, 106.68) * mm});
            skLineSegment(sketch, "E3.0.18.8", {"start": v(1913.48, 101.6) * mm, "end": v(1913.48, 5.08) * mm});
            skLineSegment(sketch, "E3.3.18.8", {"start": v(1816.96, 101.6) * mm, "end": v(1913.48, 101.6) * mm});
            skLineSegment(sketch, "E3.6.18.8", {"start": v(1816.96, 101.6) * mm, "end": v(1816.96, 5.08) * mm});
            skLineSegment(sketch, "E3.9.18.8", {"start": v(1816.96, 5.08) * mm, "end": v(1913.48, 5.08) * mm});
            skLineSegment(sketch, "E3.0.19.0", {"start": v(2014.14, 914.4) * mm, "end": v(2014.14, 817.88) * mm});
            skLineSegment(sketch, "E3.3.19.0", {"start": v(1917.62, 914.4) * mm, "end": v(2014.14, 914.4) * mm});
            skLineSegment(sketch, "E3.6.19.0", {"start": v(1917.62, 914.4) * mm, "end": v(1917.62, 817.88) * mm});
            skLineSegment(sketch, "E3.9.19.0", {"start": v(1917.62, 817.88) * mm, "end": v(2014.14, 817.88) * mm});
            skLineSegment(sketch, "E3.0.19.1", {"start": v(2014.14, 812.8) * mm, "end": v(2014.14, 716.28) * mm});
            skLineSegment(sketch, "E3.3.19.1", {"start": v(1917.62, 812.8) * mm, "end": v(2014.14, 812.8) * mm});
            skLineSegment(sketch, "E3.6.19.1", {"start": v(1917.62, 812.8) * mm, "end": v(1917.62, 716.28) * mm});
            skLineSegment(sketch, "E3.9.19.1", {"start": v(1917.62, 716.28) * mm, "end": v(2014.14, 716.28) * mm});
            skLineSegment(sketch, "E3.0.19.2", {"start": v(2014.14, 711.2) * mm, "end": v(2014.14, 614.68) * mm});
            skLineSegment(sketch, "E3.3.19.2", {"start": v(1917.62, 711.2) * mm, "end": v(2014.14, 711.2) * mm});
            skLineSegment(sketch, "E3.6.19.2", {"start": v(1917.62, 711.2) * mm, "end": v(1917.62, 614.68) * mm});
            skLineSegment(sketch, "E3.9.19.2", {"start": v(1917.62, 614.68) * mm, "end": v(2014.14, 614.68) * mm});
            skLineSegment(sketch, "E3.0.19.3", {"start": v(2014.14, 609.6) * mm, "end": v(2014.14, 513.08) * mm});
            skLineSegment(sketch, "E3.3.19.3", {"start": v(1917.62, 609.6) * mm, "end": v(2014.14, 609.6) * mm});
            skLineSegment(sketch, "E3.6.19.3", {"start": v(1917.62, 609.6) * mm, "end": v(1917.62, 513.08) * mm});
            skLineSegment(sketch, "E3.9.19.3", {"start": v(1917.62, 513.08) * mm, "end": v(2014.14, 513.08) * mm});
            skLineSegment(sketch, "E3.0.19.4", {"start": v(2014.14, 508) * mm, "end": v(2014.14, 411.48) * mm});
            skLineSegment(sketch, "E3.3.19.4", {"start": v(1917.62, 508) * mm, "end": v(2014.14, 508) * mm});
            skLineSegment(sketch, "E3.6.19.4", {"start": v(1917.62, 508) * mm, "end": v(1917.62, 411.48) * mm});
            skLineSegment(sketch, "E3.9.19.4", {"start": v(1917.62, 411.48) * mm, "end": v(2014.14, 411.48) * mm});
            skLineSegment(sketch, "E3.0.19.5", {"start": v(2014.14, 406.4) * mm, "end": v(2014.14, 309.88) * mm});
            skLineSegment(sketch, "E3.3.19.5", {"start": v(1917.62, 406.4) * mm, "end": v(2014.14, 406.4) * mm});
            skLineSegment(sketch, "E3.6.19.5", {"start": v(1917.62, 406.4) * mm, "end": v(1917.62, 309.88) * mm});
            skLineSegment(sketch, "E3.9.19.5", {"start": v(1917.62, 309.88) * mm, "end": v(2014.14, 309.88) * mm});
            skLineSegment(sketch, "E3.0.19.6", {"start": v(2014.14, 304.8) * mm, "end": v(2014.14, 208.28) * mm});
            skLineSegment(sketch, "E3.3.19.6", {"start": v(1917.62, 304.8) * mm, "end": v(2014.14, 304.8) * mm});
            skLineSegment(sketch, "E3.6.19.6", {"start": v(1917.62, 304.8) * mm, "end": v(1917.62, 208.28) * mm});
            skLineSegment(sketch, "E3.9.19.6", {"start": v(1917.62, 208.28) * mm, "end": v(2014.14, 208.28) * mm});
            skLineSegment(sketch, "E3.0.19.7", {"start": v(2014.14, 203.2) * mm, "end": v(2014.14, 106.68) * mm});
            skLineSegment(sketch, "E3.3.19.7", {"start": v(1917.62, 203.2) * mm, "end": v(2014.14, 203.2) * mm});
            skLineSegment(sketch, "E3.6.19.7", {"start": v(1917.62, 203.2) * mm, "end": v(1917.62, 106.68) * mm});
            skLineSegment(sketch, "E3.9.19.7", {"start": v(1917.62, 106.68) * mm, "end": v(2014.14, 106.68) * mm});
            skLineSegment(sketch, "E3.0.19.8", {"start": v(2014.14, 101.6) * mm, "end": v(2014.14, 5.08) * mm});
            skLineSegment(sketch, "E3.3.19.8", {"start": v(1917.62, 101.6) * mm, "end": v(2014.14, 101.6) * mm});
            skLineSegment(sketch, "E3.6.19.8", {"start": v(1917.62, 101.6) * mm, "end": v(1917.62, 5.08) * mm});
            skLineSegment(sketch, "E3.9.19.8", {"start": v(1917.62, 5.08) * mm, "end": v(2014.14, 5.08) * mm});
            skLineSegment(sketch, "E3.0.20.0", {"start": v(2114.8, 914.4) * mm, "end": v(2114.8, 817.88) * mm});
            skLineSegment(sketch, "E3.3.20.0", {"start": v(2018.28, 914.4) * mm, "end": v(2114.8, 914.4) * mm});
            skLineSegment(sketch, "E3.6.20.0", {"start": v(2018.28, 914.4) * mm, "end": v(2018.28, 817.88) * mm});
            skLineSegment(sketch, "E3.9.20.0", {"start": v(2018.28, 817.88) * mm, "end": v(2114.8, 817.88) * mm});
            skLineSegment(sketch, "E3.0.20.1", {"start": v(2114.8, 812.8) * mm, "end": v(2114.8, 716.28) * mm});
            skLineSegment(sketch, "E3.3.20.1", {"start": v(2018.28, 812.8) * mm, "end": v(2114.8, 812.8) * mm});
            skLineSegment(sketch, "E3.6.20.1", {"start": v(2018.28, 812.8) * mm, "end": v(2018.28, 716.28) * mm});
            skLineSegment(sketch, "E3.9.20.1", {"start": v(2018.28, 716.28) * mm, "end": v(2114.8, 716.28) * mm});
            skLineSegment(sketch, "E3.0.20.2", {"start": v(2114.8, 711.2) * mm, "end": v(2114.8, 614.68) * mm});
            skLineSegment(sketch, "E3.3.20.2", {"start": v(2018.28, 711.2) * mm, "end": v(2114.8, 711.2) * mm});
            skLineSegment(sketch, "E3.6.20.2", {"start": v(2018.28, 711.2) * mm, "end": v(2018.28, 614.68) * mm});
            skLineSegment(sketch, "E3.9.20.2", {"start": v(2018.28, 614.68) * mm, "end": v(2114.8, 614.68) * mm});
            skLineSegment(sketch, "E3.0.20.3", {"start": v(2114.8, 609.6) * mm, "end": v(2114.8, 513.08) * mm});
            skLineSegment(sketch, "E3.3.20.3", {"start": v(2018.28, 609.6) * mm, "end": v(2114.8, 609.6) * mm});
            skLineSegment(sketch, "E3.6.20.3", {"start": v(2018.28, 609.6) * mm, "end": v(2018.28, 513.08) * mm});
            skLineSegment(sketch, "E3.9.20.3", {"start": v(2018.28, 513.08) * mm, "end": v(2114.8, 513.08) * mm});
            skLineSegment(sketch, "E3.0.20.4", {"start": v(2114.8, 508) * mm, "end": v(2114.8, 411.48) * mm});
            skLineSegment(sketch, "E3.3.20.4", {"start": v(2018.28, 508) * mm, "end": v(2114.8, 508) * mm});
            skLineSegment(sketch, "E3.6.20.4", {"start": v(2018.28, 508) * mm, "end": v(2018.28, 411.48) * mm});
            skLineSegment(sketch, "E3.9.20.4", {"start": v(2018.28, 411.48) * mm, "end": v(2114.8, 411.48) * mm});
            skLineSegment(sketch, "E3.0.20.5", {"start": v(2114.8, 406.4) * mm, "end": v(2114.8, 309.88) * mm});
            skLineSegment(sketch, "E3.3.20.5", {"start": v(2018.28, 406.4) * mm, "end": v(2114.8, 406.4) * mm});
            skLineSegment(sketch, "E3.6.20.5", {"start": v(2018.28, 406.4) * mm, "end": v(2018.28, 309.88) * mm});
            skLineSegment(sketch, "E3.9.20.5", {"start": v(2018.28, 309.88) * mm, "end": v(2114.8, 309.88) * mm});
            skLineSegment(sketch, "E3.0.20.6", {"start": v(2114.8, 304.8) * mm, "end": v(2114.8, 208.28) * mm});
            skLineSegment(sketch, "E3.3.20.6", {"start": v(2018.28, 304.8) * mm, "end": v(2114.8, 304.8) * mm});
            skLineSegment(sketch, "E3.6.20.6", {"start": v(2018.28, 304.8) * mm, "end": v(2018.28, 208.28) * mm});
            skLineSegment(sketch, "E3.9.20.6", {"start": v(2018.28, 208.28) * mm, "end": v(2114.8, 208.28) * mm});
            skLineSegment(sketch, "E3.0.20.7", {"start": v(2114.8, 203.2) * mm, "end": v(2114.8, 106.68) * mm});
            skLineSegment(sketch, "E3.3.20.7", {"start": v(2018.28, 203.2) * mm, "end": v(2114.8, 203.2) * mm});
            skLineSegment(sketch, "E3.6.20.7", {"start": v(2018.28, 203.2) * mm, "end": v(2018.28, 106.68) * mm});
            skLineSegment(sketch, "E3.9.20.7", {"start": v(2018.28, 106.68) * mm, "end": v(2114.8, 106.68) * mm});
            skLineSegment(sketch, "E3.0.20.8", {"start": v(2114.8, 101.6) * mm, "end": v(2114.8, 5.08) * mm});
            skLineSegment(sketch, "E3.3.20.8", {"start": v(2018.28, 101.6) * mm, "end": v(2114.8, 101.6) * mm});
            skLineSegment(sketch, "E3.6.20.8", {"start": v(2018.28, 101.6) * mm, "end": v(2018.28, 5.08) * mm});
            skLineSegment(sketch, "E3.9.20.8", {"start": v(2018.28, 5.08) * mm, "end": v(2114.8, 5.08) * mm});
            skLineSegment(sketch, "E3.0.21.0", {"start": v(2215.46, 914.4) * mm, "end": v(2215.46, 817.88) * mm});
            skLineSegment(sketch, "E3.3.21.0", {"start": v(2118.94, 914.4) * mm, "end": v(2215.46, 914.4) * mm});
            skLineSegment(sketch, "E3.6.21.0", {"start": v(2118.94, 914.4) * mm, "end": v(2118.94, 817.88) * mm});
            skLineSegment(sketch, "E3.9.21.0", {"start": v(2118.94, 817.88) * mm, "end": v(2215.46, 817.88) * mm});
            skLineSegment(sketch, "E3.0.21.1", {"start": v(2215.46, 812.8) * mm, "end": v(2215.46, 716.28) * mm});
            skLineSegment(sketch, "E3.3.21.1", {"start": v(2118.94, 812.8) * mm, "end": v(2215.46, 812.8) * mm});
            skLineSegment(sketch, "E3.6.21.1", {"start": v(2118.94, 812.8) * mm, "end": v(2118.94, 716.28) * mm});
            skLineSegment(sketch, "E3.9.21.1", {"start": v(2118.94, 716.28) * mm, "end": v(2215.46, 716.28) * mm});
            skLineSegment(sketch, "E3.0.21.2", {"start": v(2215.46, 711.2) * mm, "end": v(2215.46, 614.68) * mm});
            skLineSegment(sketch, "E3.3.21.2", {"start": v(2118.94, 711.2) * mm, "end": v(2215.46, 711.2) * mm});
            skLineSegment(sketch, "E3.6.21.2", {"start": v(2118.94, 711.2) * mm, "end": v(2118.94, 614.68) * mm});
            skLineSegment(sketch, "E3.9.21.2", {"start": v(2118.94, 614.68) * mm, "end": v(2215.46, 614.68) * mm});
            skLineSegment(sketch, "E3.0.21.3", {"start": v(2215.46, 609.6) * mm, "end": v(2215.46, 513.08) * mm});
            skLineSegment(sketch, "E3.3.21.3", {"start": v(2118.94, 609.6) * mm, "end": v(2215.46, 609.6) * mm});
            skLineSegment(sketch, "E3.6.21.3", {"start": v(2118.94, 609.6) * mm, "end": v(2118.94, 513.08) * mm});
            skLineSegment(sketch, "E3.9.21.3", {"start": v(2118.94, 513.08) * mm, "end": v(2215.46, 513.08) * mm});
            skLineSegment(sketch, "E3.0.21.4", {"start": v(2215.46, 508) * mm, "end": v(2215.46, 411.48) * mm});
            skLineSegment(sketch, "E3.3.21.4", {"start": v(2118.94, 508) * mm, "end": v(2215.46, 508) * mm});
            skLineSegment(sketch, "E3.6.21.4", {"start": v(2118.94, 508) * mm, "end": v(2118.94, 411.48) * mm});
            skLineSegment(sketch, "E3.9.21.4", {"start": v(2118.94, 411.48) * mm, "end": v(2215.46, 411.48) * mm});
            skLineSegment(sketch, "E3.0.21.5", {"start": v(2215.46, 406.4) * mm, "end": v(2215.46, 309.88) * mm});
            skLineSegment(sketch, "E3.3.21.5", {"start": v(2118.94, 406.4) * mm, "end": v(2215.46, 406.4) * mm});
            skLineSegment(sketch, "E3.6.21.5", {"start": v(2118.94, 406.4) * mm, "end": v(2118.94, 309.88) * mm});
            skLineSegment(sketch, "E3.9.21.5", {"start": v(2118.94, 309.88) * mm, "end": v(2215.46, 309.88) * mm});
            skLineSegment(sketch, "E3.0.21.6", {"start": v(2215.46, 304.8) * mm, "end": v(2215.46, 208.28) * mm});
            skLineSegment(sketch, "E3.3.21.6", {"start": v(2118.94, 304.8) * mm, "end": v(2215.46, 304.8) * mm});
            skLineSegment(sketch, "E3.6.21.6", {"start": v(2118.94, 304.8) * mm, "end": v(2118.94, 208.28) * mm});
            skLineSegment(sketch, "E3.9.21.6", {"start": v(2118.94, 208.28) * mm, "end": v(2215.46, 208.28) * mm});
            skLineSegment(sketch, "E3.0.21.7", {"start": v(2215.46, 203.2) * mm, "end": v(2215.46, 106.68) * mm});
            skLineSegment(sketch, "E3.3.21.7", {"start": v(2118.94, 203.2) * mm, "end": v(2215.46, 203.2) * mm});
            skLineSegment(sketch, "E3.6.21.7", {"start": v(2118.94, 203.2) * mm, "end": v(2118.94, 106.68) * mm});
            skLineSegment(sketch, "E3.9.21.7", {"start": v(2118.94, 106.68) * mm, "end": v(2215.46, 106.68) * mm});
            skLineSegment(sketch, "E3.0.21.8", {"start": v(2215.46, 101.6) * mm, "end": v(2215.46, 5.08) * mm});
            skLineSegment(sketch, "E3.3.21.8", {"start": v(2118.94, 101.6) * mm, "end": v(2215.46, 101.6) * mm});
            skLineSegment(sketch, "E3.6.21.8", {"start": v(2118.94, 101.6) * mm, "end": v(2118.94, 5.08) * mm});
            skLineSegment(sketch, "E3.9.21.8", {"start": v(2118.94, 5.08) * mm, "end": v(2215.46, 5.08) * mm});
            skLineSegment(sketch, "E3.0.22.0", {"start": v(2316.12, 914.4) * mm, "end": v(2316.12, 817.88) * mm});
            skLineSegment(sketch, "E3.3.22.0", {"start": v(2219.6, 914.4) * mm, "end": v(2316.12, 914.4) * mm});
            skLineSegment(sketch, "E3.6.22.0", {"start": v(2219.6, 914.4) * mm, "end": v(2219.6, 817.88) * mm});
            skLineSegment(sketch, "E3.9.22.0", {"start": v(2219.6, 817.88) * mm, "end": v(2316.12, 817.88) * mm});
            skLineSegment(sketch, "E3.0.22.1", {"start": v(2316.12, 812.8) * mm, "end": v(2316.12, 716.28) * mm});
            skLineSegment(sketch, "E3.3.22.1", {"start": v(2219.6, 812.8) * mm, "end": v(2316.12, 812.8) * mm});
            skLineSegment(sketch, "E3.6.22.1", {"start": v(2219.6, 812.8) * mm, "end": v(2219.6, 716.28) * mm});
            skLineSegment(sketch, "E3.9.22.1", {"start": v(2219.6, 716.28) * mm, "end": v(2316.12, 716.28) * mm});
            skLineSegment(sketch, "E3.0.22.2", {"start": v(2316.12, 711.2) * mm, "end": v(2316.12, 614.68) * mm});
            skLineSegment(sketch, "E3.3.22.2", {"start": v(2219.6, 711.2) * mm, "end": v(2316.12, 711.2) * mm});
            skLineSegment(sketch, "E3.6.22.2", {"start": v(2219.6, 711.2) * mm, "end": v(2219.6, 614.68) * mm});
            skLineSegment(sketch, "E3.9.22.2", {"start": v(2219.6, 614.68) * mm, "end": v(2316.12, 614.68) * mm});
            skLineSegment(sketch, "E3.0.22.3", {"start": v(2316.12, 609.6) * mm, "end": v(2316.12, 513.08) * mm});
            skLineSegment(sketch, "E3.3.22.3", {"start": v(2219.6, 609.6) * mm, "end": v(2316.12, 609.6) * mm});
            skLineSegment(sketch, "E3.6.22.3", {"start": v(2219.6, 609.6) * mm, "end": v(2219.6, 513.08) * mm});
            skLineSegment(sketch, "E3.9.22.3", {"start": v(2219.6, 513.08) * mm, "end": v(2316.12, 513.08) * mm});
            skLineSegment(sketch, "E3.0.22.4", {"start": v(2316.12, 508) * mm, "end": v(2316.12, 411.48) * mm});
            skLineSegment(sketch, "E3.3.22.4", {"start": v(2219.6, 508) * mm, "end": v(2316.12, 508) * mm});
            skLineSegment(sketch, "E3.6.22.4", {"start": v(2219.6, 508) * mm, "end": v(2219.6, 411.48) * mm});
            skLineSegment(sketch, "E3.9.22.4", {"start": v(2219.6, 411.48) * mm, "end": v(2316.12, 411.48) * mm});
            skLineSegment(sketch, "E3.0.22.5", {"start": v(2316.12, 406.4) * mm, "end": v(2316.12, 309.88) * mm});
            skLineSegment(sketch, "E3.3.22.5", {"start": v(2219.6, 406.4) * mm, "end": v(2316.12, 406.4) * mm});
            skLineSegment(sketch, "E3.6.22.5", {"start": v(2219.6, 406.4) * mm, "end": v(2219.6, 309.88) * mm});
            skLineSegment(sketch, "E3.9.22.5", {"start": v(2219.6, 309.88) * mm, "end": v(2316.12, 309.88) * mm});
            skLineSegment(sketch, "E3.0.22.6", {"start": v(2316.12, 304.8) * mm, "end": v(2316.12, 208.28) * mm});
            skLineSegment(sketch, "E3.3.22.6", {"start": v(2219.6, 304.8) * mm, "end": v(2316.12, 304.8) * mm});
            skLineSegment(sketch, "E3.6.22.6", {"start": v(2219.6, 304.8) * mm, "end": v(2219.6, 208.28) * mm});
            skLineSegment(sketch, "E3.9.22.6", {"start": v(2219.6, 208.28) * mm, "end": v(2316.12, 208.28) * mm});
            skLineSegment(sketch, "E3.0.22.7", {"start": v(2316.12, 203.2) * mm, "end": v(2316.12, 106.68) * mm});
            skLineSegment(sketch, "E3.3.22.7", {"start": v(2219.6, 203.2) * mm, "end": v(2316.12, 203.2) * mm});
            skLineSegment(sketch, "E3.6.22.7", {"start": v(2219.6, 203.2) * mm, "end": v(2219.6, 106.68) * mm});
            skLineSegment(sketch, "E3.9.22.7", {"start": v(2219.6, 106.68) * mm, "end": v(2316.12, 106.68) * mm});
            skLineSegment(sketch, "E3.0.22.8", {"start": v(2316.12, 101.6) * mm, "end": v(2316.12, 5.08) * mm});
            skLineSegment(sketch, "E3.3.22.8", {"start": v(2219.6, 101.6) * mm, "end": v(2316.12, 101.6) * mm});
            skLineSegment(sketch, "E3.6.22.8", {"start": v(2219.6, 101.6) * mm, "end": v(2219.6, 5.08) * mm});
            skLineSegment(sketch, "E3.9.22.8", {"start": v(2219.6, 5.08) * mm, "end": v(2316.12, 5.08) * mm});
            skLineSegment(sketch, "E3.0.23.0", {"start": v(2416.78, 914.4) * mm, "end": v(2416.78, 817.88) * mm});
            skLineSegment(sketch, "E3.3.23.0", {"start": v(2320.26, 914.4) * mm, "end": v(2416.78, 914.4) * mm});
            skLineSegment(sketch, "E3.6.23.0", {"start": v(2320.26, 914.4) * mm, "end": v(2320.26, 817.88) * mm});
            skLineSegment(sketch, "E3.9.23.0", {"start": v(2320.26, 817.88) * mm, "end": v(2416.78, 817.88) * mm});
            skLineSegment(sketch, "E3.0.23.1", {"start": v(2416.78, 812.8) * mm, "end": v(2416.78, 716.28) * mm});
            skLineSegment(sketch, "E3.3.23.1", {"start": v(2320.26, 812.8) * mm, "end": v(2416.78, 812.8) * mm});
            skLineSegment(sketch, "E3.6.23.1", {"start": v(2320.26, 812.8) * mm, "end": v(2320.26, 716.28) * mm});
            skLineSegment(sketch, "E3.9.23.1", {"start": v(2320.26, 716.28) * mm, "end": v(2416.78, 716.28) * mm});
            skLineSegment(sketch, "E3.0.23.2", {"start": v(2416.78, 711.2) * mm, "end": v(2416.78, 614.68) * mm});
            skLineSegment(sketch, "E3.3.23.2", {"start": v(2320.26, 711.2) * mm, "end": v(2416.78, 711.2) * mm});
            skLineSegment(sketch, "E3.6.23.2", {"start": v(2320.26, 711.2) * mm, "end": v(2320.26, 614.68) * mm});
            skLineSegment(sketch, "E3.9.23.2", {"start": v(2320.26, 614.68) * mm, "end": v(2416.78, 614.68) * mm});
            skLineSegment(sketch, "E3.0.23.3", {"start": v(2416.78, 609.6) * mm, "end": v(2416.78, 513.08) * mm});
            skLineSegment(sketch, "E3.3.23.3", {"start": v(2320.26, 609.6) * mm, "end": v(2416.78, 609.6) * mm});
            skLineSegment(sketch, "E3.6.23.3", {"start": v(2320.26, 609.6) * mm, "end": v(2320.26, 513.08) * mm});
            skLineSegment(sketch, "E3.9.23.3", {"start": v(2320.26, 513.08) * mm, "end": v(2416.78, 513.08) * mm});
            skLineSegment(sketch, "E3.0.23.4", {"start": v(2416.78, 508) * mm, "end": v(2416.78, 411.48) * mm});
            skLineSegment(sketch, "E3.3.23.4", {"start": v(2320.26, 508) * mm, "end": v(2416.78, 508) * mm});
            skLineSegment(sketch, "E3.6.23.4", {"start": v(2320.26, 508) * mm, "end": v(2320.26, 411.48) * mm});
            skLineSegment(sketch, "E3.9.23.4", {"start": v(2320.26, 411.48) * mm, "end": v(2416.78, 411.48) * mm});
            skLineSegment(sketch, "E3.0.23.5", {"start": v(2416.78, 406.4) * mm, "end": v(2416.78, 309.88) * mm});
            skLineSegment(sketch, "E3.3.23.5", {"start": v(2320.26, 406.4) * mm, "end": v(2416.78, 406.4) * mm});
            skLineSegment(sketch, "E3.6.23.5", {"start": v(2320.26, 406.4) * mm, "end": v(2320.26, 309.88) * mm});
            skLineSegment(sketch, "E3.9.23.5", {"start": v(2320.26, 309.88) * mm, "end": v(2416.78, 309.88) * mm});
            skLineSegment(sketch, "E3.0.23.6", {"start": v(2416.78, 304.8) * mm, "end": v(2416.78, 208.28) * mm});
            skLineSegment(sketch, "E3.3.23.6", {"start": v(2320.26, 304.8) * mm, "end": v(2416.78, 304.8) * mm});
            skLineSegment(sketch, "E3.6.23.6", {"start": v(2320.26, 304.8) * mm, "end": v(2320.26, 208.28) * mm});
            skLineSegment(sketch, "E3.9.23.6", {"start": v(2320.26, 208.28) * mm, "end": v(2416.78, 208.28) * mm});
            skLineSegment(sketch, "E3.0.23.7", {"start": v(2416.78, 203.2) * mm, "end": v(2416.78, 106.68) * mm});
            skLineSegment(sketch, "E3.3.23.7", {"start": v(2320.26, 203.2) * mm, "end": v(2416.78, 203.2) * mm});
            skLineSegment(sketch, "E3.6.23.7", {"start": v(2320.26, 203.2) * mm, "end": v(2320.26, 106.68) * mm});
            skLineSegment(sketch, "E3.9.23.7", {"start": v(2320.26, 106.68) * mm, "end": v(2416.78, 106.68) * mm});
            skLineSegment(sketch, "E3.0.23.8", {"start": v(2416.78, 101.6) * mm, "end": v(2416.78, 5.08) * mm});
            skLineSegment(sketch, "E3.3.23.8", {"start": v(2320.26, 101.6) * mm, "end": v(2416.78, 101.6) * mm});
            skLineSegment(sketch, "E3.6.23.8", {"start": v(2320.26, 101.6) * mm, "end": v(2320.26, 5.08) * mm});
            skLineSegment(sketch, "E3.9.23.8", {"start": v(2320.26, 5.08) * mm, "end": v(2416.78, 5.08) * mm});
            skLineSegment(sketch, "E3.0.24.0", {"start": v(2517.44, 914.4) * mm, "end": v(2517.44, 817.88) * mm});
            skLineSegment(sketch, "E3.3.24.0", {"start": v(2420.92, 914.4) * mm, "end": v(2517.44, 914.4) * mm});
            skLineSegment(sketch, "E3.6.24.0", {"start": v(2420.92, 914.4) * mm, "end": v(2420.92, 817.88) * mm});
            skLineSegment(sketch, "E3.9.24.0", {"start": v(2420.92, 817.88) * mm, "end": v(2517.44, 817.88) * mm});
            skLineSegment(sketch, "E3.0.24.1", {"start": v(2517.44, 812.8) * mm, "end": v(2517.44, 716.28) * mm});
            skLineSegment(sketch, "E3.3.24.1", {"start": v(2420.92, 812.8) * mm, "end": v(2517.44, 812.8) * mm});
            skLineSegment(sketch, "E3.6.24.1", {"start": v(2420.92, 812.8) * mm, "end": v(2420.92, 716.28) * mm});
            skLineSegment(sketch, "E3.9.24.1", {"start": v(2420.92, 716.28) * mm, "end": v(2517.44, 716.28) * mm});
            skLineSegment(sketch, "E3.0.24.2", {"start": v(2517.44, 711.2) * mm, "end": v(2517.44, 614.68) * mm});
            skLineSegment(sketch, "E3.3.24.2", {"start": v(2420.92, 711.2) * mm, "end": v(2517.44, 711.2) * mm});
            skLineSegment(sketch, "E3.6.24.2", {"start": v(2420.92, 711.2) * mm, "end": v(2420.92, 614.68) * mm});
            skLineSegment(sketch, "E3.9.24.2", {"start": v(2420.92, 614.68) * mm, "end": v(2517.44, 614.68) * mm});
            skLineSegment(sketch, "E3.0.24.3", {"start": v(2517.44, 609.6) * mm, "end": v(2517.44, 513.08) * mm});
            skLineSegment(sketch, "E3.3.24.3", {"start": v(2420.92, 609.6) * mm, "end": v(2517.44, 609.6) * mm});
            skLineSegment(sketch, "E3.6.24.3", {"start": v(2420.92, 609.6) * mm, "end": v(2420.92, 513.08) * mm});
            skLineSegment(sketch, "E3.9.24.3", {"start": v(2420.92, 513.08) * mm, "end": v(2517.44, 513.08) * mm});
            skLineSegment(sketch, "E3.0.24.4", {"start": v(2517.44, 508) * mm, "end": v(2517.44, 411.48) * mm});
            skLineSegment(sketch, "E3.3.24.4", {"start": v(2420.92, 508) * mm, "end": v(2517.44, 508) * mm});
            skLineSegment(sketch, "E3.6.24.4", {"start": v(2420.92, 508) * mm, "end": v(2420.92, 411.48) * mm});
            skLineSegment(sketch, "E3.9.24.4", {"start": v(2420.92, 411.48) * mm, "end": v(2517.44, 411.48) * mm});
            skLineSegment(sketch, "E3.0.24.5", {"start": v(2517.44, 406.4) * mm, "end": v(2517.44, 309.88) * mm});
            skLineSegment(sketch, "E3.3.24.5", {"start": v(2420.92, 406.4) * mm, "end": v(2517.44, 406.4) * mm});
            skLineSegment(sketch, "E3.6.24.5", {"start": v(2420.92, 406.4) * mm, "end": v(2420.92, 309.88) * mm});
            skLineSegment(sketch, "E3.9.24.5", {"start": v(2420.92, 309.88) * mm, "end": v(2517.44, 309.88) * mm});
            skLineSegment(sketch, "E3.0.24.6", {"start": v(2517.44, 304.8) * mm, "end": v(2517.44, 208.28) * mm});
            skLineSegment(sketch, "E3.3.24.6", {"start": v(2420.92, 304.8) * mm, "end": v(2517.44, 304.8) * mm});
            skLineSegment(sketch, "E3.6.24.6", {"start": v(2420.92, 304.8) * mm, "end": v(2420.92, 208.28) * mm});
            skLineSegment(sketch, "E3.9.24.6", {"start": v(2420.92, 208.28) * mm, "end": v(2517.44, 208.28) * mm});
            skLineSegment(sketch, "E3.0.24.7", {"start": v(2517.44, 203.2) * mm, "end": v(2517.44, 106.68) * mm});
            skLineSegment(sketch, "E3.3.24.7", {"start": v(2420.92, 203.2) * mm, "end": v(2517.44, 203.2) * mm});
            skLineSegment(sketch, "E3.6.24.7", {"start": v(2420.92, 203.2) * mm, "end": v(2420.92, 106.68) * mm});
            skLineSegment(sketch, "E3.9.24.7", {"start": v(2420.92, 106.68) * mm, "end": v(2517.44, 106.68) * mm});
            skLineSegment(sketch, "E3.0.24.8", {"start": v(2517.44, 101.6) * mm, "end": v(2517.44, 5.08) * mm});
            skLineSegment(sketch, "E3.3.24.8", {"start": v(2420.92, 101.6) * mm, "end": v(2517.44, 101.6) * mm});
            skLineSegment(sketch, "E3.6.24.8", {"start": v(2420.92, 101.6) * mm, "end": v(2420.92, 5.08) * mm});
            skLineSegment(sketch, "E3.9.24.8", {"start": v(2420.92, 5.08) * mm, "end": v(2517.44, 5.08) * mm});
            skLineSegment(sketch, "E3.0.25.0", {"start": v(2618.1, 914.4) * mm, "end": v(2618.1, 817.88) * mm});
            skLineSegment(sketch, "E3.3.25.0", {"start": v(2521.59, 914.4) * mm, "end": v(2618.1, 914.4) * mm});
            skLineSegment(sketch, "E3.6.25.0", {"start": v(2521.59, 914.4) * mm, "end": v(2521.59, 817.88) * mm});
            skLineSegment(sketch, "E3.9.25.0", {"start": v(2521.59, 817.88) * mm, "end": v(2618.1, 817.88) * mm});
            skLineSegment(sketch, "E3.0.25.1", {"start": v(2618.1, 812.8) * mm, "end": v(2618.1, 716.28) * mm});
            skLineSegment(sketch, "E3.3.25.1", {"start": v(2521.59, 812.8) * mm, "end": v(2618.1, 812.8) * mm});
            skLineSegment(sketch, "E3.6.25.1", {"start": v(2521.59, 812.8) * mm, "end": v(2521.59, 716.28) * mm});
            skLineSegment(sketch, "E3.9.25.1", {"start": v(2521.59, 716.28) * mm, "end": v(2618.1, 716.28) * mm});
            skLineSegment(sketch, "E3.0.25.2", {"start": v(2618.1, 711.2) * mm, "end": v(2618.1, 614.68) * mm});
            skLineSegment(sketch, "E3.3.25.2", {"start": v(2521.59, 711.2) * mm, "end": v(2618.1, 711.2) * mm});
            skLineSegment(sketch, "E3.6.25.2", {"start": v(2521.59, 711.2) * mm, "end": v(2521.59, 614.68) * mm});
            skLineSegment(sketch, "E3.9.25.2", {"start": v(2521.59, 614.68) * mm, "end": v(2618.1, 614.68) * mm});
            skLineSegment(sketch, "E3.0.25.3", {"start": v(2618.1, 609.6) * mm, "end": v(2618.1, 513.08) * mm});
            skLineSegment(sketch, "E3.3.25.3", {"start": v(2521.59, 609.6) * mm, "end": v(2618.1, 609.6) * mm});
            skLineSegment(sketch, "E3.6.25.3", {"start": v(2521.59, 609.6) * mm, "end": v(2521.59, 513.08) * mm});
            skLineSegment(sketch, "E3.9.25.3", {"start": v(2521.59, 513.08) * mm, "end": v(2618.1, 513.08) * mm});
            skLineSegment(sketch, "E3.0.25.4", {"start": v(2618.1, 508) * mm, "end": v(2618.1, 411.48) * mm});
            skLineSegment(sketch, "E3.3.25.4", {"start": v(2521.59, 508) * mm, "end": v(2618.1, 508) * mm});
            skLineSegment(sketch, "E3.6.25.4", {"start": v(2521.59, 508) * mm, "end": v(2521.59, 411.48) * mm});
            skLineSegment(sketch, "E3.9.25.4", {"start": v(2521.59, 411.48) * mm, "end": v(2618.1, 411.48) * mm});
            skLineSegment(sketch, "E3.0.25.5", {"start": v(2618.1, 406.4) * mm, "end": v(2618.1, 309.88) * mm});
            skLineSegment(sketch, "E3.3.25.5", {"start": v(2521.59, 406.4) * mm, "end": v(2618.1, 406.4) * mm});
            skLineSegment(sketch, "E3.6.25.5", {"start": v(2521.59, 406.4) * mm, "end": v(2521.59, 309.88) * mm});
            skLineSegment(sketch, "E3.9.25.5", {"start": v(2521.59, 309.88) * mm, "end": v(2618.1, 309.88) * mm});
            skLineSegment(sketch, "E3.0.25.6", {"start": v(2618.1, 304.8) * mm, "end": v(2618.1, 208.28) * mm});
            skLineSegment(sketch, "E3.3.25.6", {"start": v(2521.59, 304.8) * mm, "end": v(2618.1, 304.8) * mm});
            skLineSegment(sketch, "E3.6.25.6", {"start": v(2521.59, 304.8) * mm, "end": v(2521.59, 208.28) * mm});
            skLineSegment(sketch, "E3.9.25.6", {"start": v(2521.59, 208.28) * mm, "end": v(2618.1, 208.28) * mm});
            skLineSegment(sketch, "E3.0.25.7", {"start": v(2618.1, 203.2) * mm, "end": v(2618.1, 106.68) * mm});
            skLineSegment(sketch, "E3.3.25.7", {"start": v(2521.59, 203.2) * mm, "end": v(2618.1, 203.2) * mm});
            skLineSegment(sketch, "E3.6.25.7", {"start": v(2521.59, 203.2) * mm, "end": v(2521.59, 106.68) * mm});
            skLineSegment(sketch, "E3.9.25.7", {"start": v(2521.59, 106.68) * mm, "end": v(2618.1, 106.68) * mm});
            skLineSegment(sketch, "E3.0.25.8", {"start": v(2618.1, 101.6) * mm, "end": v(2618.1, 5.08) * mm});
            skLineSegment(sketch, "E3.3.25.8", {"start": v(2521.59, 101.6) * mm, "end": v(2618.1, 101.6) * mm});
            skLineSegment(sketch, "E3.6.25.8", {"start": v(2521.59, 101.6) * mm, "end": v(2521.59, 5.08) * mm});
            skLineSegment(sketch, "E3.9.25.8", {"start": v(2521.59, 5.08) * mm, "end": v(2618.1, 5.08) * mm});
            skLineSegment(sketch, "E4.0.26.0", {"start": v(2718.77, 914.4) * mm, "end": v(2718.77, 817.88) * mm});
            skLineSegment(sketch, "E4.3.26.0", {"start": v(2622.25, 914.4) * mm, "end": v(2718.77, 914.4) * mm});
            skLineSegment(sketch, "E4.6.26.0", {"start": v(2622.25, 914.4) * mm, "end": v(2622.25, 817.88) * mm});
            skLineSegment(sketch, "E4.9.26.0", {"start": v(2622.25, 817.88) * mm, "end": v(2718.77, 817.88) * mm});
            skLineSegment(sketch, "E4.0.26.1", {"start": v(2718.77, 812.8) * mm, "end": v(2718.77, 716.28) * mm});
            skLineSegment(sketch, "E4.3.26.1", {"start": v(2622.25, 812.8) * mm, "end": v(2718.77, 812.8) * mm});
            skLineSegment(sketch, "E4.6.26.1", {"start": v(2622.25, 812.8) * mm, "end": v(2622.25, 716.28) * mm});
            skLineSegment(sketch, "E4.9.26.1", {"start": v(2622.25, 716.28) * mm, "end": v(2718.77, 716.28) * mm});
            skLineSegment(sketch, "E4.0.26.2", {"start": v(2718.77, 711.2) * mm, "end": v(2718.77, 614.68) * mm});
            skLineSegment(sketch, "E4.3.26.2", {"start": v(2622.25, 711.2) * mm, "end": v(2718.77, 711.2) * mm});
            skLineSegment(sketch, "E4.6.26.2", {"start": v(2622.25, 711.2) * mm, "end": v(2622.25, 614.68) * mm});
            skLineSegment(sketch, "E4.9.26.2", {"start": v(2622.25, 614.68) * mm, "end": v(2718.77, 614.68) * mm});
            skLineSegment(sketch, "E4.0.26.3", {"start": v(2718.77, 609.6) * mm, "end": v(2718.77, 513.08) * mm});
            skLineSegment(sketch, "E4.3.26.3", {"start": v(2622.25, 609.6) * mm, "end": v(2718.77, 609.6) * mm});
            skLineSegment(sketch, "E4.6.26.3", {"start": v(2622.25, 609.6) * mm, "end": v(2622.25, 513.08) * mm});
            skLineSegment(sketch, "E4.9.26.3", {"start": v(2622.25, 513.08) * mm, "end": v(2718.77, 513.08) * mm});
            skLineSegment(sketch, "E4.0.26.4", {"start": v(2718.77, 508) * mm, "end": v(2718.77, 411.48) * mm});
            skLineSegment(sketch, "E4.3.26.4", {"start": v(2622.25, 508) * mm, "end": v(2718.77, 508) * mm});
            skLineSegment(sketch, "E4.6.26.4", {"start": v(2622.25, 508) * mm, "end": v(2622.25, 411.48) * mm});
            skLineSegment(sketch, "E4.9.26.4", {"start": v(2622.25, 411.48) * mm, "end": v(2718.77, 411.48) * mm});
            skLineSegment(sketch, "E4.0.26.5", {"start": v(2718.77, 406.4) * mm, "end": v(2718.77, 309.88) * mm});
            skLineSegment(sketch, "E4.3.26.5", {"start": v(2622.25, 406.4) * mm, "end": v(2718.77, 406.4) * mm});
            skLineSegment(sketch, "E4.6.26.5", {"start": v(2622.25, 406.4) * mm, "end": v(2622.25, 309.88) * mm});
            skLineSegment(sketch, "E4.9.26.5", {"start": v(2622.25, 309.88) * mm, "end": v(2718.77, 309.88) * mm});
            skLineSegment(sketch, "E4.0.26.6", {"start": v(2718.77, 304.8) * mm, "end": v(2718.77, 208.28) * mm});
            skLineSegment(sketch, "E4.3.26.6", {"start": v(2622.25, 304.8) * mm, "end": v(2718.77, 304.8) * mm});
            skLineSegment(sketch, "E4.6.26.6", {"start": v(2622.25, 304.8) * mm, "end": v(2622.25, 208.28) * mm});
            skLineSegment(sketch, "E4.9.26.6", {"start": v(2622.25, 208.28) * mm, "end": v(2718.77, 208.28) * mm});
            skLineSegment(sketch, "E4.0.26.7", {"start": v(2718.77, 203.2) * mm, "end": v(2718.77, 106.68) * mm});
            skLineSegment(sketch, "E4.3.26.7", {"start": v(2622.25, 203.2) * mm, "end": v(2718.77, 203.2) * mm});
            skLineSegment(sketch, "E4.6.26.7", {"start": v(2622.25, 203.2) * mm, "end": v(2622.25, 106.68) * mm});
            skLineSegment(sketch, "E4.9.26.7", {"start": v(2622.25, 106.68) * mm, "end": v(2718.77, 106.68) * mm});
            skLineSegment(sketch, "E4.0.26.8", {"start": v(2718.77, 101.6) * mm, "end": v(2718.77, 5.08) * mm});
            skLineSegment(sketch, "E4.3.26.8", {"start": v(2622.25, 101.6) * mm, "end": v(2718.77, 101.6) * mm});
            skLineSegment(sketch, "E4.6.26.8", {"start": v(2622.25, 101.6) * mm, "end": v(2622.25, 5.08) * mm});
            skLineSegment(sketch, "E4.9.26.8", {"start": v(2622.25, 5.08) * mm, "end": v(2718.77, 5.08) * mm});
            skSolve(sketch);
        }
        {
            var Q0;
            Q0=qSketchRegion(id+"F2",true);
            extrude(context, id + "F3", {"entities" : qUnion([Q0]), "operationType" : NewBodyOperationType.REMOVE, "depth" : 2.54 * mm, "offsetDistance" : 25.4 * mm});
        }
    });
